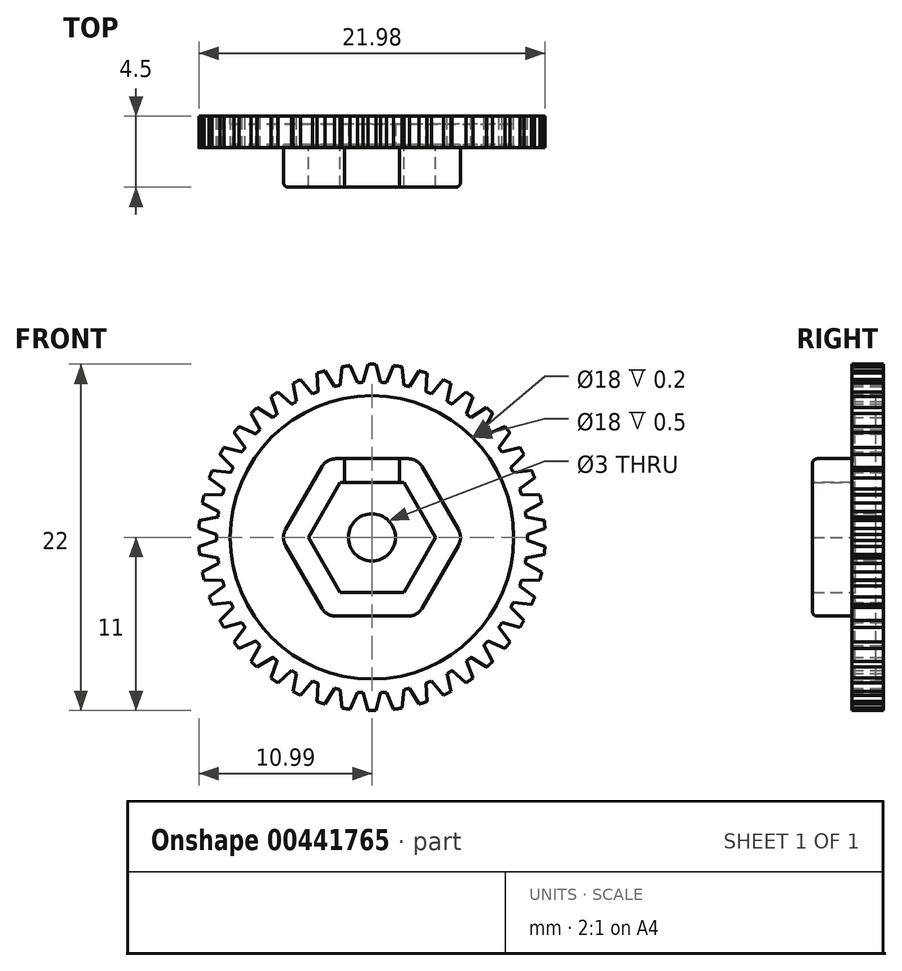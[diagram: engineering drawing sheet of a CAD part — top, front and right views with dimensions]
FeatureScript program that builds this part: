
annotation { "Feature Type Name" : "Feature", "Feature Type Description" : "" }
export const myFeature = defineFeature(function(context is Context, id is Id, definition is map)
    precondition{}
    {
        {
            var Q0;
            Q0=qCreatedBy(makeId("Front.planeOp"),FACE);
            var sketch = newSketch(context, id + "F0", { "sketchPlane" : qUnion([Q0])});
            skCircle(sketch, "E0", {"center": v(0, 0) * mm, "radius": 9.88 * mm});
            skSolve(sketch);
        }
        {
            var Q0;
            Q0=qSketchRegion(id+"F0",true);
            extrude(context, id + "F1", {"entities" : qUnion([Q0]), "depth" : 2 * mm});
        }
        {
            var Q0;
            Q0=qCreatedBy(makeId("Front.planeOp"),FACE);
            var sketch = newSketch(context, id + "F2", { "sketchPlane" : qUnion([Q0])});
            skArc(sketch, "E1", {"start": v(0, 12) * mm, "mid": v(-0.22, 12) * mm, "end": v(-0.45, 12) * mm});
            skArc(sketch, "E2", {"start": v(0.26, 11) * mm, "mid": v(-0.08, 11) * mm, "end": v(-0.41, 11) * mm});
            skArc(sketch, "E3", {"start": v(0.4, 10.5) * mm, "mid": v(0, 10.5) * mm, "end": v(-0.4, 10.5) * mm});
            skCircle(sketch, "E4", {"center": v(0, 0) * mm, "radius": 9.88 * mm});
            skLineSegment(sketch, "E5", {"start": v(0, 0) * mm, "end": v(0, 15.41) * mm});
            skLineSegment(sketch, "E6", {"start": v(0, 0) * mm, "end": v(-0.5, 13.31) * mm});
            skLineSegment(sketch, "E7", {"start": v(-0.4, 10.5) * mm, "end": v(-0.56, 9.86) * mm});
            skLineSegment(sketch, "E8", {"start": v(0.4, 10.5) * mm, "end": v(0.56, 9.86) * mm});
            skLineSegment(sketch, "E9", {"start": v(-0.4, 10.5) * mm, "end": v(-0.26, 11) * mm});
            skLineSegment(sketch, "E10", {"start": v(-0.26, 11) * mm, "end": v(0, 12) * mm});
            skLineSegment(sketch, "E11", {"start": v(0, 12) * mm, "end": v(0.26, 11) * mm});
            skLineSegment(sketch, "E12", {"start": v(0.26, 11) * mm, "end": v(0.4, 10.5) * mm});
            skLineSegment(sketch, "E13.1.0", {"start": v(-1.95, 10.32) * mm, "end": v(-2.02, 9.67) * mm});
            skLineSegment(sketch, "E13.1.1", {"start": v(-1.95, 10.32) * mm, "end": v(-1.9, 10.84) * mm});
            skLineSegment(sketch, "E13.1.2", {"start": v(-1.38, 10.91) * mm, "end": v(-1.18, 10.43) * mm});
            skLineSegment(sketch, "E13.1.3", {"start": v(-1.18, 10.43) * mm, "end": v(-0.92, 9.83) * mm});
            skArc(sketch, "E13.1.4", {"start": v(-1.38, 10.91) * mm, "mid": v(-1.71, 10.87) * mm, "end": v(-2.05, 10.8) * mm});
            skLineSegment(sketch, "E13.2.0", {"start": v(-3.47, 9.91) * mm, "end": v(-3.44, 9.26) * mm});
            skLineSegment(sketch, "E13.2.1", {"start": v(-3.47, 9.91) * mm, "end": v(-3.5, 10.43) * mm});
            skLineSegment(sketch, "E13.2.2", {"start": v(-3, 10.59) * mm, "end": v(-2.72, 10.14) * mm});
            skLineSegment(sketch, "E13.2.3", {"start": v(-2.72, 10.14) * mm, "end": v(-2.37, 9.59) * mm});
            skArc(sketch, "E13.2.4", {"start": v(-3, 10.59) * mm, "mid": v(-3.31, 10.49) * mm, "end": v(-3.63, 10.38) * mm});
            skLineSegment(sketch, "E13.3.0", {"start": v(-4.9, 9.28) * mm, "end": v(-4.78, 8.64) * mm});
            skLineSegment(sketch, "E13.3.1", {"start": v(-4.9, 9.28) * mm, "end": v(-5, 9.8) * mm});
            skLineSegment(sketch, "E13.3.2", {"start": v(-4.54, 10.02) * mm, "end": v(-4.2, 9.62) * mm});
            skLineSegment(sketch, "E13.3.3", {"start": v(-4.2, 9.62) * mm, "end": v(-3.78, 9.12) * mm});
            skArc(sketch, "E13.3.4", {"start": v(-4.54, 10.02) * mm, "mid": v(-4.84, 9.88) * mm, "end": v(-5.14, 9.73) * mm});
            skLineSegment(sketch, "E13.4.0", {"start": v(-6.24, 8.45) * mm, "end": v(-6.01, 7.83) * mm});
            skLineSegment(sketch, "E13.4.1", {"start": v(-6.24, 8.45) * mm, "end": v(-6.41, 8.94) * mm});
            skLineSegment(sketch, "E13.4.2", {"start": v(-5.98, 9.23) * mm, "end": v(-5.59, 8.9) * mm});
            skLineSegment(sketch, "E13.4.3", {"start": v(-5.59, 8.9) * mm, "end": v(-5.1, 8.46) * mm});
            skArc(sketch, "E13.4.4", {"start": v(-5.98, 9.23) * mm, "mid": v(-6.26, 9.05) * mm, "end": v(-6.53, 8.85) * mm});
            skLineSegment(sketch, "E13.5.0", {"start": v(-7.42, 7.42) * mm, "end": v(-7.11, 6.85) * mm});
            skLineSegment(sketch, "E13.5.1", {"start": v(-7.42, 7.42) * mm, "end": v(-7.67, 7.88) * mm});
            skLineSegment(sketch, "E13.5.2", {"start": v(-7.29, 8.24) * mm, "end": v(-6.85, 7.96) * mm});
            skLineSegment(sketch, "E13.5.3", {"start": v(-6.85, 7.96) * mm, "end": v(-6.3, 7.6) * mm});
            skArc(sketch, "E13.5.4", {"start": v(-7.29, 8.24) * mm, "mid": v(-7.54, 8.01) * mm, "end": v(-7.78, 7.78) * mm});
            skLineSegment(sketch, "E13.6.0", {"start": v(-8.45, 6.24) * mm, "end": v(-8.06, 5.71) * mm});
            skLineSegment(sketch, "E13.6.1", {"start": v(-8.45, 6.24) * mm, "end": v(-8.76, 6.65) * mm});
            skLineSegment(sketch, "E13.6.2", {"start": v(-8.43, 7.06) * mm, "end": v(-7.96, 6.85) * mm});
            skLineSegment(sketch, "E13.6.3", {"start": v(-7.96, 6.85) * mm, "end": v(-7.36, 6.58) * mm});
            skArc(sketch, "E13.6.4", {"start": v(-8.43, 7.06) * mm, "mid": v(-8.65, 6.8) * mm, "end": v(-8.85, 6.53) * mm});
            skLineSegment(sketch, "E13.7.0", {"start": v(-9.28, 4.9) * mm, "end": v(-8.82, 4.45) * mm});
            skLineSegment(sketch, "E13.7.1", {"start": v(-9.28, 4.9) * mm, "end": v(-9.65, 5.27) * mm});
            skLineSegment(sketch, "E13.7.2", {"start": v(-9.4, 5.72) * mm, "end": v(-8.9, 5.59) * mm});
            skLineSegment(sketch, "E13.7.3", {"start": v(-8.9, 5.59) * mm, "end": v(-8.26, 5.41) * mm});
            skArc(sketch, "E13.7.4", {"start": v(-9.4, 5.72) * mm, "mid": v(-9.56, 5.43) * mm, "end": v(-9.73, 5.14) * mm});
            skLineSegment(sketch, "E13.8.0", {"start": v(-9.91, 3.47) * mm, "end": v(-9.38, 3.08) * mm});
            skLineSegment(sketch, "E13.8.1", {"start": v(-9.91, 3.47) * mm, "end": v(-10.33, 3.77) * mm});
            skLineSegment(sketch, "E13.8.2", {"start": v(-10.14, 4.26) * mm, "end": v(-9.62, 4.2) * mm});
            skLineSegment(sketch, "E13.8.3", {"start": v(-9.62, 4.2) * mm, "end": v(-8.97, 4.12) * mm});
            skArc(sketch, "E13.8.4", {"start": v(-10.14, 4.26) * mm, "mid": v(-10.27, 3.95) * mm, "end": v(-10.38, 3.63) * mm});
            skLineSegment(sketch, "E13.9.0", {"start": v(-10.32, 1.95) * mm, "end": v(-9.74, 1.65) * mm});
            skLineSegment(sketch, "E13.9.1", {"start": v(-10.32, 1.95) * mm, "end": v(-10.78, 2.2) * mm});
            skLineSegment(sketch, "E13.9.2", {"start": v(-10.66, 2.7) * mm, "end": v(-10.14, 2.72) * mm});
            skLineSegment(sketch, "E13.9.3", {"start": v(-10.14, 2.72) * mm, "end": v(-9.49, 2.74) * mm});
            skArc(sketch, "E13.9.4", {"start": v(-10.66, 2.7) * mm, "mid": v(-10.74, 2.37) * mm, "end": v(-10.8, 2.05) * mm});
            skLineSegment(sketch, "E13.10.0", {"start": v(-10.5, 0.4) * mm, "end": v(-9.87, 0.18) * mm});
            skLineSegment(sketch, "E13.10.1", {"start": v(-10.5, 0.4) * mm, "end": v(-10.99, 0.56) * mm});
            skLineSegment(sketch, "E13.10.2", {"start": v(-10.95, 1.08) * mm, "end": v(-10.43, 1.18) * mm});
            skLineSegment(sketch, "E13.10.3", {"start": v(-10.43, 1.18) * mm, "end": v(-9.8, 1.3) * mm});
            skArc(sketch, "E13.10.4", {"start": v(-10.95, 1.08) * mm, "mid": v(-10.97, 0.75) * mm, "end": v(-11, 0.41) * mm});
            skLineSegment(sketch, "E13.11.0", {"start": v(-10.43, -1.18) * mm, "end": v(-9.8, -1.3) * mm});
            skLineSegment(sketch, "E13.11.1", {"start": v(-10.43, -1.18) * mm, "end": v(-10.95, -1.08) * mm});
            skLineSegment(sketch, "E13.11.2", {"start": v(-10.99, -0.56) * mm, "end": v(-10.5, -0.4) * mm});
            skLineSegment(sketch, "E13.11.3", {"start": v(-10.5, -0.4) * mm, "end": v(-9.87, -0.18) * mm});
            skArc(sketch, "E13.11.4", {"start": v(-10.99, -0.56) * mm, "mid": v(-10.96, -0.9) * mm, "end": v(-10.93, -1.23) * mm});
            skLineSegment(sketch, "E13.12.0", {"start": v(-10.14, -2.72) * mm, "end": v(-9.49, -2.74) * mm});
            skLineSegment(sketch, "E13.12.1", {"start": v(-10.14, -2.72) * mm, "end": v(-10.66, -2.7) * mm});
            skLineSegment(sketch, "E13.12.2", {"start": v(-10.78, -2.2) * mm, "end": v(-10.32, -1.95) * mm});
            skLineSegment(sketch, "E13.12.3", {"start": v(-10.32, -1.95) * mm, "end": v(-9.74, -1.65) * mm});
            skArc(sketch, "E13.12.4", {"start": v(-10.78, -2.2) * mm, "mid": v(-10.7, -2.52) * mm, "end": v(-10.63, -2.85) * mm});
            skLineSegment(sketch, "E13.13.0", {"start": v(-9.62, -4.2) * mm, "end": v(-8.97, -4.12) * mm});
            skLineSegment(sketch, "E13.13.1", {"start": v(-9.62, -4.2) * mm, "end": v(-10.14, -4.26) * mm});
            skLineSegment(sketch, "E13.13.2", {"start": v(-10.33, -3.77) * mm, "end": v(-9.91, -3.47) * mm});
            skLineSegment(sketch, "E13.13.3", {"start": v(-9.91, -3.47) * mm, "end": v(-9.38, -3.08) * mm});
            skArc(sketch, "E13.13.4", {"start": v(-10.33, -3.77) * mm, "mid": v(-10.21, -4.09) * mm, "end": v(-10.08, -4.4) * mm});
            skLineSegment(sketch, "E13.14.0", {"start": v(-8.9, -5.59) * mm, "end": v(-8.26, -5.41) * mm});
            skLineSegment(sketch, "E13.14.1", {"start": v(-8.9, -5.59) * mm, "end": v(-9.4, -5.72) * mm});
            skLineSegment(sketch, "E13.14.2", {"start": v(-9.65, -5.27) * mm, "end": v(-9.28, -4.9) * mm});
            skLineSegment(sketch, "E13.14.3", {"start": v(-9.28, -4.9) * mm, "end": v(-8.82, -4.45) * mm});
            skArc(sketch, "E13.14.4", {"start": v(-9.65, -5.27) * mm, "mid": v(-9.49, -5.56) * mm, "end": v(-9.31, -5.85) * mm});
            skLineSegment(sketch, "E13.15.0", {"start": v(-7.96, -6.85) * mm, "end": v(-7.36, -6.58) * mm});
            skLineSegment(sketch, "E13.15.1", {"start": v(-7.96, -6.85) * mm, "end": v(-8.43, -7.06) * mm});
            skLineSegment(sketch, "E13.15.2", {"start": v(-8.76, -6.65) * mm, "end": v(-8.45, -6.24) * mm});
            skLineSegment(sketch, "E13.15.3", {"start": v(-8.45, -6.24) * mm, "end": v(-8.06, -5.71) * mm});
            skArc(sketch, "E13.15.4", {"start": v(-8.76, -6.65) * mm, "mid": v(-8.55, -6.92) * mm, "end": v(-8.34, -7.18) * mm});
            skLineSegment(sketch, "E13.16.0", {"start": v(-6.85, -7.96) * mm, "end": v(-6.3, -7.6) * mm});
            skLineSegment(sketch, "E13.16.1", {"start": v(-6.85, -7.96) * mm, "end": v(-7.29, -8.24) * mm});
            skLineSegment(sketch, "E13.16.2", {"start": v(-7.67, -7.88) * mm, "end": v(-7.42, -7.42) * mm});
            skLineSegment(sketch, "E13.16.3", {"start": v(-7.42, -7.42) * mm, "end": v(-7.11, -6.85) * mm});
            skArc(sketch, "E13.16.4", {"start": v(-7.67, -7.88) * mm, "mid": v(-7.43, -8.11) * mm, "end": v(-7.18, -8.34) * mm});
            skLineSegment(sketch, "E13.17.0", {"start": v(-5.59, -8.9) * mm, "end": v(-5.1, -8.46) * mm});
            skLineSegment(sketch, "E13.17.1", {"start": v(-5.59, -8.9) * mm, "end": v(-5.98, -9.23) * mm});
            skLineSegment(sketch, "E13.17.2", {"start": v(-6.41, -8.94) * mm, "end": v(-6.24, -8.45) * mm});
            skLineSegment(sketch, "E13.17.3", {"start": v(-6.24, -8.45) * mm, "end": v(-6.01, -7.83) * mm});
            skArc(sketch, "E13.17.4", {"start": v(-6.41, -8.94) * mm, "mid": v(-6.13, -9.13) * mm, "end": v(-5.85, -9.31) * mm});
            skLineSegment(sketch, "E13.18.0", {"start": v(-4.2, -9.62) * mm, "end": v(-3.78, -9.12) * mm});
            skLineSegment(sketch, "E13.18.1", {"start": v(-4.2, -9.62) * mm, "end": v(-4.54, -10.02) * mm});
            skLineSegment(sketch, "E13.18.2", {"start": v(-5, -9.8) * mm, "end": v(-4.9, -9.28) * mm});
            skLineSegment(sketch, "E13.18.3", {"start": v(-4.9, -9.28) * mm, "end": v(-4.78, -8.64) * mm});
            skArc(sketch, "E13.18.4", {"start": v(-5, -9.8) * mm, "mid": v(-4.7, -9.94) * mm, "end": v(-4.4, -10.08) * mm});
            skLineSegment(sketch, "E13.19.0", {"start": v(-2.72, -10.14) * mm, "end": v(-2.37, -9.59) * mm});
            skLineSegment(sketch, "E13.19.1", {"start": v(-2.72, -10.14) * mm, "end": v(-3, -10.59) * mm});
            skLineSegment(sketch, "E13.19.2", {"start": v(-3.5, -10.43) * mm, "end": v(-3.47, -9.91) * mm});
            skLineSegment(sketch, "E13.19.3", {"start": v(-3.47, -9.91) * mm, "end": v(-3.44, -9.26) * mm});
            skArc(sketch, "E13.19.4", {"start": v(-3.5, -10.43) * mm, "mid": v(-3.17, -10.53) * mm, "end": v(-2.85, -10.63) * mm});
            skLineSegment(sketch, "E13.20.0", {"start": v(-1.18, -10.43) * mm, "end": v(-0.92, -9.83) * mm});
            skLineSegment(sketch, "E13.20.1", {"start": v(-1.18, -10.43) * mm, "end": v(-1.38, -10.91) * mm});
            skLineSegment(sketch, "E13.20.2", {"start": v(-1.9, -10.84) * mm, "end": v(-1.95, -10.32) * mm});
            skLineSegment(sketch, "E13.20.3", {"start": v(-1.95, -10.32) * mm, "end": v(-2.02, -9.67) * mm});
            skArc(sketch, "E13.20.4", {"start": v(-1.9, -10.84) * mm, "mid": v(-1.57, -10.89) * mm, "end": v(-1.23, -10.93) * mm});
            skLineSegment(sketch, "E13.21.0", {"start": v(0.4, -10.5) * mm, "end": v(0.56, -9.86) * mm});
            skLineSegment(sketch, "E13.21.1", {"start": v(0.4, -10.5) * mm, "end": v(0.26, -11) * mm});
            skLineSegment(sketch, "E13.21.2", {"start": v(-0.26, -11) * mm, "end": v(-0.4, -10.5) * mm});
            skLineSegment(sketch, "E13.21.3", {"start": v(-0.4, -10.5) * mm, "end": v(-0.56, -9.86) * mm});
            skArc(sketch, "E13.21.4", {"start": v(-0.26, -11) * mm, "mid": v(0.08, -11) * mm, "end": v(0.41, -11) * mm});
            skLineSegment(sketch, "E13.22.0", {"start": v(1.95, -10.32) * mm, "end": v(2.02, -9.67) * mm});
            skLineSegment(sketch, "E13.22.1", {"start": v(1.95, -10.32) * mm, "end": v(1.9, -10.84) * mm});
            skLineSegment(sketch, "E13.22.2", {"start": v(1.38, -10.91) * mm, "end": v(1.18, -10.43) * mm});
            skLineSegment(sketch, "E13.22.3", {"start": v(1.18, -10.43) * mm, "end": v(0.92, -9.83) * mm});
            skArc(sketch, "E13.22.4", {"start": v(1.38, -10.91) * mm, "mid": v(1.71, -10.87) * mm, "end": v(2.05, -10.8) * mm});
            skLineSegment(sketch, "E13.23.0", {"start": v(3.47, -9.91) * mm, "end": v(3.44, -9.26) * mm});
            skLineSegment(sketch, "E13.23.1", {"start": v(3.47, -9.91) * mm, "end": v(3.5, -10.43) * mm});
            skLineSegment(sketch, "E13.23.2", {"start": v(3, -10.59) * mm, "end": v(2.72, -10.14) * mm});
            skLineSegment(sketch, "E13.23.3", {"start": v(2.72, -10.14) * mm, "end": v(2.37, -9.59) * mm});
            skArc(sketch, "E13.23.4", {"start": v(3, -10.59) * mm, "mid": v(3.31, -10.49) * mm, "end": v(3.63, -10.38) * mm});
            skLineSegment(sketch, "E13.24.0", {"start": v(4.9, -9.28) * mm, "end": v(4.78, -8.64) * mm});
            skLineSegment(sketch, "E13.24.1", {"start": v(4.9, -9.28) * mm, "end": v(5, -9.8) * mm});
            skLineSegment(sketch, "E13.24.2", {"start": v(4.54, -10.02) * mm, "end": v(4.2, -9.62) * mm});
            skLineSegment(sketch, "E13.24.3", {"start": v(4.2, -9.62) * mm, "end": v(3.78, -9.12) * mm});
            skArc(sketch, "E13.24.4", {"start": v(4.54, -10.02) * mm, "mid": v(4.84, -9.88) * mm, "end": v(5.14, -9.73) * mm});
            skLineSegment(sketch, "E13.25.0", {"start": v(6.24, -8.45) * mm, "end": v(6.01, -7.83) * mm});
            skLineSegment(sketch, "E13.25.1", {"start": v(6.24, -8.45) * mm, "end": v(6.41, -8.94) * mm});
            skLineSegment(sketch, "E13.25.2", {"start": v(5.98, -9.23) * mm, "end": v(5.59, -8.9) * mm});
            skLineSegment(sketch, "E13.25.3", {"start": v(5.59, -8.9) * mm, "end": v(5.1, -8.46) * mm});
            skArc(sketch, "E13.25.4", {"start": v(5.98, -9.23) * mm, "mid": v(6.26, -9.05) * mm, "end": v(6.53, -8.85) * mm});
            skLineSegment(sketch, "E13.26.0", {"start": v(7.42, -7.42) * mm, "end": v(7.11, -6.85) * mm});
            skLineSegment(sketch, "E13.26.1", {"start": v(7.42, -7.42) * mm, "end": v(7.67, -7.88) * mm});
            skLineSegment(sketch, "E13.26.2", {"start": v(7.29, -8.24) * mm, "end": v(6.85, -7.96) * mm});
            skLineSegment(sketch, "E13.26.3", {"start": v(6.85, -7.96) * mm, "end": v(6.3, -7.6) * mm});
            skArc(sketch, "E13.26.4", {"start": v(7.29, -8.24) * mm, "mid": v(7.54, -8.01) * mm, "end": v(7.78, -7.78) * mm});
            skLineSegment(sketch, "E13.27.0", {"start": v(8.45, -6.24) * mm, "end": v(8.06, -5.71) * mm});
            skLineSegment(sketch, "E13.27.1", {"start": v(8.45, -6.24) * mm, "end": v(8.76, -6.65) * mm});
            skLineSegment(sketch, "E13.27.2", {"start": v(8.43, -7.06) * mm, "end": v(7.96, -6.85) * mm});
            skLineSegment(sketch, "E13.27.3", {"start": v(7.96, -6.85) * mm, "end": v(7.36, -6.58) * mm});
            skArc(sketch, "E13.27.4", {"start": v(8.43, -7.06) * mm, "mid": v(8.65, -6.8) * mm, "end": v(8.85, -6.53) * mm});
            skLineSegment(sketch, "E13.28.0", {"start": v(9.28, -4.9) * mm, "end": v(8.82, -4.45) * mm});
            skLineSegment(sketch, "E13.28.1", {"start": v(9.28, -4.9) * mm, "end": v(9.65, -5.27) * mm});
            skLineSegment(sketch, "E13.28.2", {"start": v(9.4, -5.72) * mm, "end": v(8.9, -5.59) * mm});
            skLineSegment(sketch, "E13.28.3", {"start": v(8.9, -5.59) * mm, "end": v(8.26, -5.41) * mm});
            skArc(sketch, "E13.28.4", {"start": v(9.4, -5.72) * mm, "mid": v(9.56, -5.43) * mm, "end": v(9.73, -5.14) * mm});
            skLineSegment(sketch, "E13.29.0", {"start": v(9.91, -3.47) * mm, "end": v(9.38, -3.08) * mm});
            skLineSegment(sketch, "E13.29.1", {"start": v(9.91, -3.47) * mm, "end": v(10.33, -3.77) * mm});
            skLineSegment(sketch, "E13.29.2", {"start": v(10.14, -4.26) * mm, "end": v(9.62, -4.2) * mm});
            skLineSegment(sketch, "E13.29.3", {"start": v(9.62, -4.2) * mm, "end": v(8.97, -4.12) * mm});
            skArc(sketch, "E13.29.4", {"start": v(10.14, -4.26) * mm, "mid": v(10.27, -3.95) * mm, "end": v(10.38, -3.63) * mm});
            skLineSegment(sketch, "E13.30.0", {"start": v(10.32, -1.95) * mm, "end": v(9.74, -1.65) * mm});
            skLineSegment(sketch, "E13.30.1", {"start": v(10.32, -1.95) * mm, "end": v(10.78, -2.2) * mm});
            skLineSegment(sketch, "E13.30.2", {"start": v(10.66, -2.7) * mm, "end": v(10.14, -2.72) * mm});
            skLineSegment(sketch, "E13.30.3", {"start": v(10.14, -2.72) * mm, "end": v(9.49, -2.74) * mm});
            skArc(sketch, "E13.30.4", {"start": v(10.66, -2.7) * mm, "mid": v(10.74, -2.37) * mm, "end": v(10.8, -2.05) * mm});
            skLineSegment(sketch, "E13.31.0", {"start": v(10.5, -0.4) * mm, "end": v(9.87, -0.18) * mm});
            skLineSegment(sketch, "E13.31.1", {"start": v(10.5, -0.4) * mm, "end": v(10.99, -0.56) * mm});
            skLineSegment(sketch, "E13.31.2", {"start": v(10.95, -1.08) * mm, "end": v(10.43, -1.18) * mm});
            skLineSegment(sketch, "E13.31.3", {"start": v(10.43, -1.18) * mm, "end": v(9.8, -1.3) * mm});
            skArc(sketch, "E13.31.4", {"start": v(10.95, -1.08) * mm, "mid": v(10.97, -0.75) * mm, "end": v(11, -0.41) * mm});
            skLineSegment(sketch, "E13.32.0", {"start": v(10.43, 1.18) * mm, "end": v(9.8, 1.3) * mm});
            skLineSegment(sketch, "E13.32.1", {"start": v(10.43, 1.18) * mm, "end": v(10.95, 1.08) * mm});
            skLineSegment(sketch, "E13.32.2", {"start": v(10.99, 0.56) * mm, "end": v(10.5, 0.4) * mm});
            skLineSegment(sketch, "E13.32.3", {"start": v(10.5, 0.4) * mm, "end": v(9.87, 0.18) * mm});
            skArc(sketch, "E13.32.4", {"start": v(10.99, 0.56) * mm, "mid": v(10.96, 0.9) * mm, "end": v(10.93, 1.23) * mm});
            skLineSegment(sketch, "E13.33.0", {"start": v(10.14, 2.72) * mm, "end": v(9.49, 2.74) * mm});
            skLineSegment(sketch, "E13.33.1", {"start": v(10.14, 2.72) * mm, "end": v(10.66, 2.7) * mm});
            skLineSegment(sketch, "E13.33.2", {"start": v(10.78, 2.2) * mm, "end": v(10.32, 1.95) * mm});
            skLineSegment(sketch, "E13.33.3", {"start": v(10.32, 1.95) * mm, "end": v(9.74, 1.65) * mm});
            skArc(sketch, "E13.33.4", {"start": v(10.78, 2.2) * mm, "mid": v(10.7, 2.52) * mm, "end": v(10.63, 2.85) * mm});
            skLineSegment(sketch, "E13.34.0", {"start": v(9.62, 4.2) * mm, "end": v(8.97, 4.12) * mm});
            skLineSegment(sketch, "E13.34.1", {"start": v(9.62, 4.2) * mm, "end": v(10.14, 4.26) * mm});
            skLineSegment(sketch, "E13.34.2", {"start": v(10.33, 3.77) * mm, "end": v(9.91, 3.47) * mm});
            skLineSegment(sketch, "E13.34.3", {"start": v(9.91, 3.47) * mm, "end": v(9.38, 3.08) * mm});
            skArc(sketch, "E13.34.4", {"start": v(10.33, 3.77) * mm, "mid": v(10.21, 4.09) * mm, "end": v(10.08, 4.4) * mm});
            skLineSegment(sketch, "E13.35.0", {"start": v(8.9, 5.59) * mm, "end": v(8.26, 5.41) * mm});
            skLineSegment(sketch, "E13.35.1", {"start": v(8.9, 5.59) * mm, "end": v(9.4, 5.72) * mm});
            skLineSegment(sketch, "E13.35.2", {"start": v(9.65, 5.27) * mm, "end": v(9.28, 4.9) * mm});
            skLineSegment(sketch, "E13.35.3", {"start": v(9.28, 4.9) * mm, "end": v(8.82, 4.45) * mm});
            skArc(sketch, "E13.35.4", {"start": v(9.65, 5.27) * mm, "mid": v(9.49, 5.56) * mm, "end": v(9.31, 5.85) * mm});
            skLineSegment(sketch, "E13.36.0", {"start": v(7.96, 6.85) * mm, "end": v(7.36, 6.58) * mm});
            skLineSegment(sketch, "E13.36.1", {"start": v(7.96, 6.85) * mm, "end": v(8.43, 7.06) * mm});
            skLineSegment(sketch, "E13.36.2", {"start": v(8.76, 6.65) * mm, "end": v(8.45, 6.24) * mm});
            skLineSegment(sketch, "E13.36.3", {"start": v(8.45, 6.24) * mm, "end": v(8.06, 5.71) * mm});
            skArc(sketch, "E13.36.4", {"start": v(8.76, 6.65) * mm, "mid": v(8.55, 6.92) * mm, "end": v(8.34, 7.18) * mm});
            skLineSegment(sketch, "E13.37.0", {"start": v(6.85, 7.96) * mm, "end": v(6.3, 7.6) * mm});
            skLineSegment(sketch, "E13.37.1", {"start": v(6.85, 7.96) * mm, "end": v(7.29, 8.24) * mm});
            skLineSegment(sketch, "E13.37.2", {"start": v(7.67, 7.88) * mm, "end": v(7.42, 7.42) * mm});
            skLineSegment(sketch, "E13.37.3", {"start": v(7.42, 7.42) * mm, "end": v(7.11, 6.85) * mm});
            skArc(sketch, "E13.37.4", {"start": v(7.67, 7.88) * mm, "mid": v(7.43, 8.11) * mm, "end": v(7.18, 8.34) * mm});
            skLineSegment(sketch, "E13.38.0", {"start": v(5.59, 8.9) * mm, "end": v(5.1, 8.46) * mm});
            skLineSegment(sketch, "E13.38.1", {"start": v(5.59, 8.9) * mm, "end": v(5.98, 9.23) * mm});
            skLineSegment(sketch, "E13.38.2", {"start": v(6.41, 8.94) * mm, "end": v(6.24, 8.45) * mm});
            skLineSegment(sketch, "E13.38.3", {"start": v(6.24, 8.45) * mm, "end": v(6.01, 7.83) * mm});
            skArc(sketch, "E13.38.4", {"start": v(6.41, 8.94) * mm, "mid": v(6.13, 9.13) * mm, "end": v(5.85, 9.31) * mm});
            skLineSegment(sketch, "E13.39.0", {"start": v(4.2, 9.62) * mm, "end": v(3.78, 9.12) * mm});
            skLineSegment(sketch, "E13.39.1", {"start": v(4.2, 9.62) * mm, "end": v(4.54, 10.02) * mm});
            skLineSegment(sketch, "E13.39.2", {"start": v(5, 9.8) * mm, "end": v(4.9, 9.28) * mm});
            skLineSegment(sketch, "E13.39.3", {"start": v(4.9, 9.28) * mm, "end": v(4.78, 8.64) * mm});
            skArc(sketch, "E13.39.4", {"start": v(5, 9.8) * mm, "mid": v(4.7, 9.94) * mm, "end": v(4.4, 10.08) * mm});
            skLineSegment(sketch, "E13.40.0", {"start": v(2.72, 10.14) * mm, "end": v(2.37, 9.59) * mm});
            skLineSegment(sketch, "E13.40.1", {"start": v(2.72, 10.14) * mm, "end": v(3, 10.59) * mm});
            skLineSegment(sketch, "E13.40.2", {"start": v(3.5, 10.43) * mm, "end": v(3.47, 9.91) * mm});
            skLineSegment(sketch, "E13.40.3", {"start": v(3.47, 9.91) * mm, "end": v(3.44, 9.26) * mm});
            skArc(sketch, "E13.40.4", {"start": v(3.5, 10.43) * mm, "mid": v(3.17, 10.53) * mm, "end": v(2.85, 10.63) * mm});
            skLineSegment(sketch, "E13.41.0", {"start": v(1.18, 10.43) * mm, "end": v(0.92, 9.83) * mm});
            skLineSegment(sketch, "E13.41.1", {"start": v(1.18, 10.43) * mm, "end": v(1.38, 10.91) * mm});
            skLineSegment(sketch, "E13.41.2", {"start": v(1.9, 10.84) * mm, "end": v(1.95, 10.32) * mm});
            skLineSegment(sketch, "E13.41.3", {"start": v(1.95, 10.32) * mm, "end": v(2.02, 9.67) * mm});
            skArc(sketch, "E13.41.4", {"start": v(1.9, 10.84) * mm, "mid": v(1.57, 10.89) * mm, "end": v(1.23, 10.93) * mm});
            skSolve(sketch);
        }
        {
            var Q0;
            {var subQ2=sQuery(id+"F2.wireOp",EDGE,"E13.32.0");Q0=makeQuery(id+"F2.imprint","IMPRINT",FACE,{"disambiguationData":[TD([[makeQuery(id+"F2.imprint","IMPRINT",EDGE,{"derivedFrom":subQ2}),1.0]])]});}
            var Q1;
            {var subQ1=sQuery(id+"F2.wireOp",EDGE,"E13.33.0");Q1=makeQuery(id+"F2.imprint","IMPRINT",FACE,{"disambiguationData":[TD([[makeQuery(id+"F2.imprint","IMPRINT",EDGE,{"derivedFrom":subQ1}),1.0]])]});}
            var Q2;
            {var subQ2=sQuery(id+"F2.wireOp",EDGE,"E13.34.0");Q2=makeQuery(id+"F2.imprint","IMPRINT",FACE,{"disambiguationData":[TD([[makeQuery(id+"F2.imprint","IMPRINT",EDGE,{"derivedFrom":subQ2}),1.0]])]});}
            var Q3;
            {var subQ1=sQuery(id+"F2.wireOp",EDGE,"E13.35.0");Q3=makeQuery(id+"F2.imprint","IMPRINT",FACE,{"disambiguationData":[TD([[makeQuery(id+"F2.imprint","IMPRINT",EDGE,{"derivedFrom":subQ1}),1.0]])]});}
            var Q4;
            {var subQ2=sQuery(id+"F2.wireOp",EDGE,"E13.36.0");Q4=makeQuery(id+"F2.imprint","IMPRINT",FACE,{"disambiguationData":[TD([[makeQuery(id+"F2.imprint","IMPRINT",EDGE,{"derivedFrom":subQ2}),1.0]])]});}
            var Q5;
            {var subQ2=sQuery(id+"F2.wireOp",EDGE,"E13.37.0");Q5=makeQuery(id+"F2.imprint","IMPRINT",FACE,{"disambiguationData":[TD([[makeQuery(id+"F2.imprint","IMPRINT",EDGE,{"derivedFrom":subQ2}),1.0]])]});}
            var Q6;
            {var subQ1=sQuery(id+"F2.wireOp",EDGE,"E13.38.0");Q6=makeQuery(id+"F2.imprint","IMPRINT",FACE,{"disambiguationData":[TD([[makeQuery(id+"F2.imprint","IMPRINT",EDGE,{"derivedFrom":subQ1}),1.0]])]});}
            var Q7;
            {var subQ2=sQuery(id+"F2.wireOp",EDGE,"E13.39.0");Q7=makeQuery(id+"F2.imprint","IMPRINT",FACE,{"disambiguationData":[TD([[makeQuery(id+"F2.imprint","IMPRINT",EDGE,{"derivedFrom":subQ2}),1.0]])]});}
            var Q8;
            {var subQ1=sQuery(id+"F2.wireOp",EDGE,"E13.40.0");Q8=makeQuery(id+"F2.imprint","IMPRINT",FACE,{"disambiguationData":[TD([[makeQuery(id+"F2.imprint","IMPRINT",EDGE,{"derivedFrom":subQ1}),1.0]])]});}
            var Q9;
            {var subQ2=sQuery(id+"F2.wireOp",EDGE,"E13.41.0");Q9=makeQuery(id+"F2.imprint","IMPRINT",FACE,{"disambiguationData":[TD([[makeQuery(id+"F2.imprint","IMPRINT",EDGE,{"derivedFrom":subQ2}),1.0]])]});}
            var Q10;
            {var subQ2=sQuery(id+"F2.wireOp",EDGE,"E13.1.0");Q10=makeQuery(id+"F2.imprint","IMPRINT",FACE,{"disambiguationData":[TD([[makeQuery(id+"F2.imprint","IMPRINT",EDGE,{"derivedFrom":subQ2}),1.0]])]});}
            var Q11;
            {var subQ1=sQuery(id+"F2.wireOp",EDGE,"E13.2.0");Q11=makeQuery(id+"F2.imprint","IMPRINT",FACE,{"disambiguationData":[TD([[makeQuery(id+"F2.imprint","IMPRINT",EDGE,{"derivedFrom":subQ1}),1.0]])]});}
            var Q12;
            {var subQ2=sQuery(id+"F2.wireOp",EDGE,"E13.3.0");Q12=makeQuery(id+"F2.imprint","IMPRINT",FACE,{"disambiguationData":[TD([[makeQuery(id+"F2.imprint","IMPRINT",EDGE,{"derivedFrom":subQ2}),1.0]])]});}
            var Q13;
            {var subQ2=sQuery(id+"F2.wireOp",EDGE,"E13.4.0");Q13=makeQuery(id+"F2.imprint","IMPRINT",FACE,{"disambiguationData":[TD([[makeQuery(id+"F2.imprint","IMPRINT",EDGE,{"derivedFrom":subQ2}),1.0]])]});}
            var Q14;
            {var subQ1=sQuery(id+"F2.wireOp",EDGE,"E13.5.0");Q14=makeQuery(id+"F2.imprint","IMPRINT",FACE,{"disambiguationData":[TD([[makeQuery(id+"F2.imprint","IMPRINT",EDGE,{"derivedFrom":subQ1}),1.0]])]});}
            var Q15;
            {var subQ2=sQuery(id+"F2.wireOp",EDGE,"E13.6.0");Q15=makeQuery(id+"F2.imprint","IMPRINT",FACE,{"disambiguationData":[TD([[makeQuery(id+"F2.imprint","IMPRINT",EDGE,{"derivedFrom":subQ2}),1.0]])]});}
            var Q16;
            {var subQ1=sQuery(id+"F2.wireOp",EDGE,"E13.7.0");Q16=makeQuery(id+"F2.imprint","IMPRINT",FACE,{"disambiguationData":[TD([[makeQuery(id+"F2.imprint","IMPRINT",EDGE,{"derivedFrom":subQ1}),1.0]])]});}
            var Q17;
            {var subQ1=sQuery(id+"F2.wireOp",EDGE,"E13.8.0");Q17=makeQuery(id+"F2.imprint","IMPRINT",FACE,{"disambiguationData":[TD([[makeQuery(id+"F2.imprint","IMPRINT",EDGE,{"derivedFrom":subQ1}),1.0]])]});}
            var Q18;
            {var subQ2=sQuery(id+"F2.wireOp",EDGE,"E13.9.0");Q18=makeQuery(id+"F2.imprint","IMPRINT",FACE,{"disambiguationData":[TD([[makeQuery(id+"F2.imprint","IMPRINT",EDGE,{"derivedFrom":subQ2}),1.0]])]});}
            var Q19;
            {var subQ1=sQuery(id+"F2.wireOp",EDGE,"E13.10.0");Q19=makeQuery(id+"F2.imprint","IMPRINT",FACE,{"disambiguationData":[TD([[makeQuery(id+"F2.imprint","IMPRINT",EDGE,{"derivedFrom":subQ1}),1.0]])]});}
            var Q20;
            {var subQ2=sQuery(id+"F2.wireOp",EDGE,"E13.11.0");Q20=makeQuery(id+"F2.imprint","IMPRINT",FACE,{"disambiguationData":[TD([[makeQuery(id+"F2.imprint","IMPRINT",EDGE,{"derivedFrom":subQ2}),1.0]])]});}
            var Q21;
            {var subQ1=sQuery(id+"F2.wireOp",EDGE,"E13.12.0");Q21=makeQuery(id+"F2.imprint","IMPRINT",FACE,{"disambiguationData":[TD([[makeQuery(id+"F2.imprint","IMPRINT",EDGE,{"derivedFrom":subQ1}),1.0]])]});}
            var Q22;
            {var subQ2=sQuery(id+"F2.wireOp",EDGE,"E13.13.0");Q22=makeQuery(id+"F2.imprint","IMPRINT",FACE,{"disambiguationData":[TD([[makeQuery(id+"F2.imprint","IMPRINT",EDGE,{"derivedFrom":subQ2}),1.0]])]});}
            var Q23;
            {var subQ2=sQuery(id+"F2.wireOp",EDGE,"E13.14.0");Q23=makeQuery(id+"F2.imprint","IMPRINT",FACE,{"disambiguationData":[TD([[makeQuery(id+"F2.imprint","IMPRINT",EDGE,{"derivedFrom":subQ2}),1.0]])]});}
            var Q24;
            {var subQ1=sQuery(id+"F2.wireOp",EDGE,"E13.15.0");Q24=makeQuery(id+"F2.imprint","IMPRINT",FACE,{"disambiguationData":[TD([[makeQuery(id+"F2.imprint","IMPRINT",EDGE,{"derivedFrom":subQ1}),1.0]])]});}
            var Q25;
            {var subQ2=sQuery(id+"F2.wireOp",EDGE,"E13.16.0");Q25=makeQuery(id+"F2.imprint","IMPRINT",FACE,{"disambiguationData":[TD([[makeQuery(id+"F2.imprint","IMPRINT",EDGE,{"derivedFrom":subQ2}),1.0]])]});}
            var Q26;
            {var subQ1=sQuery(id+"F2.wireOp",EDGE,"E13.17.0");Q26=makeQuery(id+"F2.imprint","IMPRINT",FACE,{"disambiguationData":[TD([[makeQuery(id+"F2.imprint","IMPRINT",EDGE,{"derivedFrom":subQ1}),1.0]])]});}
            var Q27;
            {var subQ2=sQuery(id+"F2.wireOp",EDGE,"E13.18.0");Q27=makeQuery(id+"F2.imprint","IMPRINT",FACE,{"disambiguationData":[TD([[makeQuery(id+"F2.imprint","IMPRINT",EDGE,{"derivedFrom":subQ2}),1.0]])]});}
            var Q28;
            {var subQ1=sQuery(id+"F2.wireOp",EDGE,"E13.19.0");Q28=makeQuery(id+"F2.imprint","IMPRINT",FACE,{"disambiguationData":[TD([[makeQuery(id+"F2.imprint","IMPRINT",EDGE,{"derivedFrom":subQ1}),1.0]])]});}
            var Q29;
            {var subQ1=sQuery(id+"F2.wireOp",EDGE,"E13.20.0");Q29=makeQuery(id+"F2.imprint","IMPRINT",FACE,{"disambiguationData":[TD([[makeQuery(id+"F2.imprint","IMPRINT",EDGE,{"derivedFrom":subQ1}),1.0]])]});}
            var Q30;
            {var subQ2=sQuery(id+"F2.wireOp",EDGE,"E13.21.0");Q30=makeQuery(id+"F2.imprint","IMPRINT",FACE,{"disambiguationData":[TD([[makeQuery(id+"F2.imprint","IMPRINT",EDGE,{"derivedFrom":subQ2}),1.0]])]});}
            var Q31;
            {var subQ1=sQuery(id+"F2.wireOp",EDGE,"E13.22.0");Q31=makeQuery(id+"F2.imprint","IMPRINT",FACE,{"disambiguationData":[TD([[makeQuery(id+"F2.imprint","IMPRINT",EDGE,{"derivedFrom":subQ1}),1.0]])]});}
            var Q32;
            {var subQ2=sQuery(id+"F2.wireOp",EDGE,"E13.23.0");Q32=makeQuery(id+"F2.imprint","IMPRINT",FACE,{"disambiguationData":[TD([[makeQuery(id+"F2.imprint","IMPRINT",EDGE,{"derivedFrom":subQ2}),1.0]])]});}
            var Q33;
            {var subQ2=sQuery(id+"F2.wireOp",EDGE,"E13.24.0");Q33=makeQuery(id+"F2.imprint","IMPRINT",FACE,{"disambiguationData":[TD([[makeQuery(id+"F2.imprint","IMPRINT",EDGE,{"derivedFrom":subQ2}),1.0]])]});}
            var Q34;
            {var subQ1=sQuery(id+"F2.wireOp",EDGE,"E13.25.0");Q34=makeQuery(id+"F2.imprint","IMPRINT",FACE,{"disambiguationData":[TD([[makeQuery(id+"F2.imprint","IMPRINT",EDGE,{"derivedFrom":subQ1}),1.0]])]});}
            var Q35;
            {var subQ2=sQuery(id+"F2.wireOp",EDGE,"E13.26.0");Q35=makeQuery(id+"F2.imprint","IMPRINT",FACE,{"disambiguationData":[TD([[makeQuery(id+"F2.imprint","IMPRINT",EDGE,{"derivedFrom":subQ2}),1.0]])]});}
            var Q36;
            {var subQ1=sQuery(id+"F2.wireOp",EDGE,"E13.27.0");Q36=makeQuery(id+"F2.imprint","IMPRINT",FACE,{"disambiguationData":[TD([[makeQuery(id+"F2.imprint","IMPRINT",EDGE,{"derivedFrom":subQ1}),1.0]])]});}
            var Q37;
            {var subQ2=sQuery(id+"F2.wireOp",EDGE,"E13.28.0");Q37=makeQuery(id+"F2.imprint","IMPRINT",FACE,{"disambiguationData":[TD([[makeQuery(id+"F2.imprint","IMPRINT",EDGE,{"derivedFrom":subQ2}),1.0]])]});}
            var Q38;
            {var subQ2=sQuery(id+"F2.wireOp",EDGE,"E13.29.0");Q38=makeQuery(id+"F2.imprint","IMPRINT",FACE,{"disambiguationData":[TD([[makeQuery(id+"F2.imprint","IMPRINT",EDGE,{"derivedFrom":subQ2}),1.0]])]});}
            var Q39;
            {var subQ1=sQuery(id+"F2.wireOp",EDGE,"E13.30.0");Q39=makeQuery(id+"F2.imprint","IMPRINT",FACE,{"disambiguationData":[TD([[makeQuery(id+"F2.imprint","IMPRINT",EDGE,{"derivedFrom":subQ1}),1.0]])]});}
            var Q40;
            {var subQ2=sQuery(id+"F2.wireOp",EDGE,"E13.31.0");Q40=makeQuery(id+"F2.imprint","IMPRINT",FACE,{"disambiguationData":[TD([[makeQuery(id+"F2.imprint","IMPRINT",EDGE,{"derivedFrom":subQ2}),1.0]])]});}
            var Q41;
            {var subQ0=sQuery(id+"F2.wireOp",EDGE,"E7");Q41=makeQuery(id+"F2.imprint","IMPRINT",FACE,{"disambiguationData":[TD([[makeQuery(id+"F2.imprint","IMPRINT",EDGE,{"derivedFrom":subQ0}),1.0]])]});}
            var Q42;
            {var subQ0=sQuery(id+"F2.wireOp",EDGE,"E12");Q42=makeQuery(id+"F2.imprint","IMPRINT",FACE,{"disambiguationData":[TD([[makeQuery(id+"F2.imprint","IMPRINT",EDGE,{"derivedFrom":subQ0}),-1.0]])]});}
            var Q43;
            {var subQ0=sQuery(id+"F2.wireOp",EDGE,"E8");Q43=makeQuery(id+"F2.imprint","IMPRINT",FACE,{"disambiguationData":[TD([[makeQuery(id+"F2.imprint","IMPRINT",EDGE,{"derivedFrom":subQ0}),-1.0]])]});}
            var Q44;
            {var subQ0=sQuery(id+"F2.wireOp",EDGE,"E9");Q44=makeQuery(id+"F2.imprint","IMPRINT",FACE,{"disambiguationData":[TD([[makeQuery(id+"F2.imprint","IMPRINT",EDGE,{"derivedFrom":subQ0}),-1.0]])]});}
            var Q45;
            {var subQ3=sQuery(id+"F2.wireOp",EDGE,"E5");var subQ5=sQuery(id+"F2.wireOp",EDGE,"E4");var subQ6=makeQuery(id+"F2.imprint","INTERSECT",VERTEX,{"derivedFrom":[subQ5,subQ3]});Q45=makeQuery(id+"F2.imprint","IMPRINT",FACE,{"disambiguationData":[TD([[makeQuery(id+"F2.imprint","IMPRINT",EDGE,{"disambiguationData":[TD([[subQ6,-1.0]])],"derivedFrom":subQ5}),-1.0]])]});}
            extrude(context, id + "F3", {"entities" : qUnion([Q0, Q1, Q2, Q3, Q4, Q5, Q6, Q7, Q8, Q9, Q10, Q11, Q12, Q13, Q14, Q15, Q16, Q17, Q18, Q19, Q20, Q21, Q22, Q23, Q24, Q25, Q26, Q27, Q28, Q29, Q30, Q31, Q32, Q33, Q34, Q35, Q36, Q37, Q38, Q39, Q40, Q41, Q42, Q43, Q44, Q45]), "operationType" : NewBodyOperationType.ADD, "depth" : 2 * mm});
        }
        {
            var Q0;
            {var subQ0=sQuery(id+"F2.wireOp",EDGE,"E4");Q0=makeQuery(id+"F3.boolean.opBoolean","MERGE",FACE,{"derivedFrom":[makeQuery(id+"F1.opExtrude","CAP_FACE",FACE,{"disambiguationData":[OSD([sQuery(id+"F0.wireOp",EDGE,"E0")])],"isStart":false}),makeQuery(id+"F3.opExtrude","CAP_FACE",FACE,{"disambiguationData":[OSD([sQuery(id+"F2.wireOp",EDGE,"E2"),subQ0,sQuery(id+"F2.wireOp",EDGE,"E7"),sQuery(id+"F2.wireOp",EDGE,"E8"),sQuery(id+"F2.wireOp",EDGE,"E9"),sQuery(id+"F2.wireOp",EDGE,"E12")])],"isStart":false}),makeQuery(id+"F3.opExtrude","CAP_FACE",FACE,{"disambiguationData":[OSD([subQ0,sQuery(id+"F2.wireOp",EDGE,"E13.32.0"),sQuery(id+"F2.wireOp",EDGE,"E13.32.1"),sQuery(id+"F2.wireOp",EDGE,"E13.32.2"),sQuery(id+"F2.wireOp",EDGE,"E13.32.3"),sQuery(id+"F2.wireOp",EDGE,"E13.32.4")])],"isStart":false}),makeQuery(id+"F3.opExtrude","CAP_FACE",FACE,{"disambiguationData":[OSD([subQ0,sQuery(id+"F2.wireOp",EDGE,"E13.33.0"),sQuery(id+"F2.wireOp",EDGE,"E13.33.1"),sQuery(id+"F2.wireOp",EDGE,"E13.33.2"),sQuery(id+"F2.wireOp",EDGE,"E13.33.3"),sQuery(id+"F2.wireOp",EDGE,"E13.33.4")])],"isStart":false}),makeQuery(id+"F3.opExtrude","CAP_FACE",FACE,{"disambiguationData":[OSD([subQ0,sQuery(id+"F2.wireOp",EDGE,"E13.34.0"),sQuery(id+"F2.wireOp",EDGE,"E13.34.1"),sQuery(id+"F2.wireOp",EDGE,"E13.34.2"),sQuery(id+"F2.wireOp",EDGE,"E13.34.3"),sQuery(id+"F2.wireOp",EDGE,"E13.34.4")])],"isStart":false}),makeQuery(id+"F3.opExtrude","CAP_FACE",FACE,{"disambiguationData":[OSD([subQ0,sQuery(id+"F2.wireOp",EDGE,"E13.35.0"),sQuery(id+"F2.wireOp",EDGE,"E13.35.1"),sQuery(id+"F2.wireOp",EDGE,"E13.35.2"),sQuery(id+"F2.wireOp",EDGE,"E13.35.3"),sQuery(id+"F2.wireOp",EDGE,"E13.35.4")])],"isStart":false}),makeQuery(id+"F3.opExtrude","CAP_FACE",FACE,{"disambiguationData":[OSD([subQ0,sQuery(id+"F2.wireOp",EDGE,"E13.36.0"),sQuery(id+"F2.wireOp",EDGE,"E13.36.1"),sQuery(id+"F2.wireOp",EDGE,"E13.36.2"),sQuery(id+"F2.wireOp",EDGE,"E13.36.3"),sQuery(id+"F2.wireOp",EDGE,"E13.36.4")])],"isStart":false}),makeQuery(id+"F3.opExtrude","CAP_FACE",FACE,{"disambiguationData":[OSD([subQ0,sQuery(id+"F2.wireOp",EDGE,"E13.37.0"),sQuery(id+"F2.wireOp",EDGE,"E13.37.1"),sQuery(id+"F2.wireOp",EDGE,"E13.37.2"),sQuery(id+"F2.wireOp",EDGE,"E13.37.3"),sQuery(id+"F2.wireOp",EDGE,"E13.37.4")])],"isStart":false}),makeQuery(id+"F3.opExtrude","CAP_FACE",FACE,{"disambiguationData":[OSD([subQ0,sQuery(id+"F2.wireOp",EDGE,"E13.38.0"),sQuery(id+"F2.wireOp",EDGE,"E13.38.1"),sQuery(id+"F2.wireOp",EDGE,"E13.38.2"),sQuery(id+"F2.wireOp",EDGE,"E13.38.3"),sQuery(id+"F2.wireOp",EDGE,"E13.38.4")])],"isStart":false}),makeQuery(id+"F3.opExtrude","CAP_FACE",FACE,{"disambiguationData":[OSD([subQ0,sQuery(id+"F2.wireOp",EDGE,"E13.39.0"),sQuery(id+"F2.wireOp",EDGE,"E13.39.1"),sQuery(id+"F2.wireOp",EDGE,"E13.39.2"),sQuery(id+"F2.wireOp",EDGE,"E13.39.3"),sQuery(id+"F2.wireOp",EDGE,"E13.39.4")])],"isStart":false}),makeQuery(id+"F3.opExtrude","CAP_FACE",FACE,{"disambiguationData":[OSD([subQ0,sQuery(id+"F2.wireOp",EDGE,"E13.40.0"),sQuery(id+"F2.wireOp",EDGE,"E13.40.1"),sQuery(id+"F2.wireOp",EDGE,"E13.40.2"),sQuery(id+"F2.wireOp",EDGE,"E13.40.3"),sQuery(id+"F2.wireOp",EDGE,"E13.40.4")])],"isStart":false}),makeQuery(id+"F3.opExtrude","CAP_FACE",FACE,{"disambiguationData":[OSD([subQ0,sQuery(id+"F2.wireOp",EDGE,"E13.41.0"),sQuery(id+"F2.wireOp",EDGE,"E13.41.1"),sQuery(id+"F2.wireOp",EDGE,"E13.41.2"),sQuery(id+"F2.wireOp",EDGE,"E13.41.3"),sQuery(id+"F2.wireOp",EDGE,"E13.41.4")])],"isStart":false}),makeQuery(id+"F3.opExtrude","CAP_FACE",FACE,{"disambiguationData":[OSD([subQ0,sQuery(id+"F2.wireOp",EDGE,"E13.1.0"),sQuery(id+"F2.wireOp",EDGE,"E13.1.1"),sQuery(id+"F2.wireOp",EDGE,"E13.1.2"),sQuery(id+"F2.wireOp",EDGE,"E13.1.3"),sQuery(id+"F2.wireOp",EDGE,"E13.1.4")])],"isStart":false}),makeQuery(id+"F3.opExtrude","CAP_FACE",FACE,{"disambiguationData":[OSD([subQ0,sQuery(id+"F2.wireOp",EDGE,"E13.2.0"),sQuery(id+"F2.wireOp",EDGE,"E13.2.1"),sQuery(id+"F2.wireOp",EDGE,"E13.2.2"),sQuery(id+"F2.wireOp",EDGE,"E13.2.3"),sQuery(id+"F2.wireOp",EDGE,"E13.2.4")])],"isStart":false}),makeQuery(id+"F3.opExtrude","CAP_FACE",FACE,{"disambiguationData":[OSD([subQ0,sQuery(id+"F2.wireOp",EDGE,"E13.3.0"),sQuery(id+"F2.wireOp",EDGE,"E13.3.1"),sQuery(id+"F2.wireOp",EDGE,"E13.3.2"),sQuery(id+"F2.wireOp",EDGE,"E13.3.3"),sQuery(id+"F2.wireOp",EDGE,"E13.3.4")])],"isStart":false}),makeQuery(id+"F3.opExtrude","CAP_FACE",FACE,{"disambiguationData":[OSD([subQ0,sQuery(id+"F2.wireOp",EDGE,"E13.4.0"),sQuery(id+"F2.wireOp",EDGE,"E13.4.1"),sQuery(id+"F2.wireOp",EDGE,"E13.4.2"),sQuery(id+"F2.wireOp",EDGE,"E13.4.3"),sQuery(id+"F2.wireOp",EDGE,"E13.4.4")])],"isStart":false}),makeQuery(id+"F3.opExtrude","CAP_FACE",FACE,{"disambiguationData":[OSD([subQ0,sQuery(id+"F2.wireOp",EDGE,"E13.5.0"),sQuery(id+"F2.wireOp",EDGE,"E13.5.1"),sQuery(id+"F2.wireOp",EDGE,"E13.5.2"),sQuery(id+"F2.wireOp",EDGE,"E13.5.3"),sQuery(id+"F2.wireOp",EDGE,"E13.5.4")])],"isStart":false}),makeQuery(id+"F3.opExtrude","CAP_FACE",FACE,{"disambiguationData":[OSD([subQ0,sQuery(id+"F2.wireOp",EDGE,"E13.6.0"),sQuery(id+"F2.wireOp",EDGE,"E13.6.1"),sQuery(id+"F2.wireOp",EDGE,"E13.6.2"),sQuery(id+"F2.wireOp",EDGE,"E13.6.3"),sQuery(id+"F2.wireOp",EDGE,"E13.6.4")])],"isStart":false}),makeQuery(id+"F3.opExtrude","CAP_FACE",FACE,{"disambiguationData":[OSD([subQ0,sQuery(id+"F2.wireOp",EDGE,"E13.7.0"),sQuery(id+"F2.wireOp",EDGE,"E13.7.1"),sQuery(id+"F2.wireOp",EDGE,"E13.7.2"),sQuery(id+"F2.wireOp",EDGE,"E13.7.3"),sQuery(id+"F2.wireOp",EDGE,"E13.7.4")])],"isStart":false}),makeQuery(id+"F3.opExtrude","CAP_FACE",FACE,{"disambiguationData":[OSD([subQ0,sQuery(id+"F2.wireOp",EDGE,"E13.8.0"),sQuery(id+"F2.wireOp",EDGE,"E13.8.1"),sQuery(id+"F2.wireOp",EDGE,"E13.8.2"),sQuery(id+"F2.wireOp",EDGE,"E13.8.3"),sQuery(id+"F2.wireOp",EDGE,"E13.8.4")])],"isStart":false}),makeQuery(id+"F3.opExtrude","CAP_FACE",FACE,{"disambiguationData":[OSD([subQ0,sQuery(id+"F2.wireOp",EDGE,"E13.9.0"),sQuery(id+"F2.wireOp",EDGE,"E13.9.1"),sQuery(id+"F2.wireOp",EDGE,"E13.9.2"),sQuery(id+"F2.wireOp",EDGE,"E13.9.3"),sQuery(id+"F2.wireOp",EDGE,"E13.9.4")])],"isStart":false}),makeQuery(id+"F3.opExtrude","CAP_FACE",FACE,{"disambiguationData":[OSD([subQ0,sQuery(id+"F2.wireOp",EDGE,"E13.10.0"),sQuery(id+"F2.wireOp",EDGE,"E13.10.1"),sQuery(id+"F2.wireOp",EDGE,"E13.10.2"),sQuery(id+"F2.wireOp",EDGE,"E13.10.3"),sQuery(id+"F2.wireOp",EDGE,"E13.10.4")])],"isStart":false}),makeQuery(id+"F3.opExtrude","CAP_FACE",FACE,{"disambiguationData":[OSD([subQ0,sQuery(id+"F2.wireOp",EDGE,"E13.11.0"),sQuery(id+"F2.wireOp",EDGE,"E13.11.1"),sQuery(id+"F2.wireOp",EDGE,"E13.11.2"),sQuery(id+"F2.wireOp",EDGE,"E13.11.3"),sQuery(id+"F2.wireOp",EDGE,"E13.11.4")])],"isStart":false}),makeQuery(id+"F3.opExtrude","CAP_FACE",FACE,{"disambiguationData":[OSD([subQ0,sQuery(id+"F2.wireOp",EDGE,"E13.12.0"),sQuery(id+"F2.wireOp",EDGE,"E13.12.1"),sQuery(id+"F2.wireOp",EDGE,"E13.12.2"),sQuery(id+"F2.wireOp",EDGE,"E13.12.3"),sQuery(id+"F2.wireOp",EDGE,"E13.12.4")])],"isStart":false}),makeQuery(id+"F3.opExtrude","CAP_FACE",FACE,{"disambiguationData":[OSD([subQ0,sQuery(id+"F2.wireOp",EDGE,"E13.13.0"),sQuery(id+"F2.wireOp",EDGE,"E13.13.1"),sQuery(id+"F2.wireOp",EDGE,"E13.13.2"),sQuery(id+"F2.wireOp",EDGE,"E13.13.3"),sQuery(id+"F2.wireOp",EDGE,"E13.13.4")])],"isStart":false}),makeQuery(id+"F3.opExtrude","CAP_FACE",FACE,{"disambiguationData":[OSD([subQ0,sQuery(id+"F2.wireOp",EDGE,"E13.14.0"),sQuery(id+"F2.wireOp",EDGE,"E13.14.1"),sQuery(id+"F2.wireOp",EDGE,"E13.14.2"),sQuery(id+"F2.wireOp",EDGE,"E13.14.3"),sQuery(id+"F2.wireOp",EDGE,"E13.14.4")])],"isStart":false}),makeQuery(id+"F3.opExtrude","CAP_FACE",FACE,{"disambiguationData":[OSD([subQ0,sQuery(id+"F2.wireOp",EDGE,"E13.15.0"),sQuery(id+"F2.wireOp",EDGE,"E13.15.1"),sQuery(id+"F2.wireOp",EDGE,"E13.15.2"),sQuery(id+"F2.wireOp",EDGE,"E13.15.3"),sQuery(id+"F2.wireOp",EDGE,"E13.15.4")])],"isStart":false}),makeQuery(id+"F3.opExtrude","CAP_FACE",FACE,{"disambiguationData":[OSD([subQ0,sQuery(id+"F2.wireOp",EDGE,"E13.16.0"),sQuery(id+"F2.wireOp",EDGE,"E13.16.1"),sQuery(id+"F2.wireOp",EDGE,"E13.16.2"),sQuery(id+"F2.wireOp",EDGE,"E13.16.3"),sQuery(id+"F2.wireOp",EDGE,"E13.16.4")])],"isStart":false}),makeQuery(id+"F3.opExtrude","CAP_FACE",FACE,{"disambiguationData":[OSD([subQ0,sQuery(id+"F2.wireOp",EDGE,"E13.17.0"),sQuery(id+"F2.wireOp",EDGE,"E13.17.1"),sQuery(id+"F2.wireOp",EDGE,"E13.17.2"),sQuery(id+"F2.wireOp",EDGE,"E13.17.3"),sQuery(id+"F2.wireOp",EDGE,"E13.17.4")])],"isStart":false}),makeQuery(id+"F3.opExtrude","CAP_FACE",FACE,{"disambiguationData":[OSD([subQ0,sQuery(id+"F2.wireOp",EDGE,"E13.18.0"),sQuery(id+"F2.wireOp",EDGE,"E13.18.1"),sQuery(id+"F2.wireOp",EDGE,"E13.18.2"),sQuery(id+"F2.wireOp",EDGE,"E13.18.3"),sQuery(id+"F2.wireOp",EDGE,"E13.18.4")])],"isStart":false}),makeQuery(id+"F3.opExtrude","CAP_FACE",FACE,{"disambiguationData":[OSD([subQ0,sQuery(id+"F2.wireOp",EDGE,"E13.19.0"),sQuery(id+"F2.wireOp",EDGE,"E13.19.1"),sQuery(id+"F2.wireOp",EDGE,"E13.19.2"),sQuery(id+"F2.wireOp",EDGE,"E13.19.3"),sQuery(id+"F2.wireOp",EDGE,"E13.19.4")])],"isStart":false}),makeQuery(id+"F3.opExtrude","CAP_FACE",FACE,{"disambiguationData":[OSD([subQ0,sQuery(id+"F2.wireOp",EDGE,"E13.20.0"),sQuery(id+"F2.wireOp",EDGE,"E13.20.1"),sQuery(id+"F2.wireOp",EDGE,"E13.20.2"),sQuery(id+"F2.wireOp",EDGE,"E13.20.3"),sQuery(id+"F2.wireOp",EDGE,"E13.20.4")])],"isStart":false}),makeQuery(id+"F3.opExtrude","CAP_FACE",FACE,{"disambiguationData":[OSD([subQ0,sQuery(id+"F2.wireOp",EDGE,"E13.21.0"),sQuery(id+"F2.wireOp",EDGE,"E13.21.1"),sQuery(id+"F2.wireOp",EDGE,"E13.21.2"),sQuery(id+"F2.wireOp",EDGE,"E13.21.3"),sQuery(id+"F2.wireOp",EDGE,"E13.21.4")])],"isStart":false}),makeQuery(id+"F3.opExtrude","CAP_FACE",FACE,{"disambiguationData":[OSD([subQ0,sQuery(id+"F2.wireOp",EDGE,"E13.22.0"),sQuery(id+"F2.wireOp",EDGE,"E13.22.1"),sQuery(id+"F2.wireOp",EDGE,"E13.22.2"),sQuery(id+"F2.wireOp",EDGE,"E13.22.3"),sQuery(id+"F2.wireOp",EDGE,"E13.22.4")])],"isStart":false}),makeQuery(id+"F3.opExtrude","CAP_FACE",FACE,{"disambiguationData":[OSD([subQ0,sQuery(id+"F2.wireOp",EDGE,"E13.23.0"),sQuery(id+"F2.wireOp",EDGE,"E13.23.1"),sQuery(id+"F2.wireOp",EDGE,"E13.23.2"),sQuery(id+"F2.wireOp",EDGE,"E13.23.3"),sQuery(id+"F2.wireOp",EDGE,"E13.23.4")])],"isStart":false}),makeQuery(id+"F3.opExtrude","CAP_FACE",FACE,{"disambiguationData":[OSD([subQ0,sQuery(id+"F2.wireOp",EDGE,"E13.24.0"),sQuery(id+"F2.wireOp",EDGE,"E13.24.1"),sQuery(id+"F2.wireOp",EDGE,"E13.24.2"),sQuery(id+"F2.wireOp",EDGE,"E13.24.3"),sQuery(id+"F2.wireOp",EDGE,"E13.24.4")])],"isStart":false}),makeQuery(id+"F3.opExtrude","CAP_FACE",FACE,{"disambiguationData":[OSD([subQ0,sQuery(id+"F2.wireOp",EDGE,"E13.25.0"),sQuery(id+"F2.wireOp",EDGE,"E13.25.1"),sQuery(id+"F2.wireOp",EDGE,"E13.25.2"),sQuery(id+"F2.wireOp",EDGE,"E13.25.3"),sQuery(id+"F2.wireOp",EDGE,"E13.25.4")])],"isStart":false}),makeQuery(id+"F3.opExtrude","CAP_FACE",FACE,{"disambiguationData":[OSD([subQ0,sQuery(id+"F2.wireOp",EDGE,"E13.26.0"),sQuery(id+"F2.wireOp",EDGE,"E13.26.1"),sQuery(id+"F2.wireOp",EDGE,"E13.26.2"),sQuery(id+"F2.wireOp",EDGE,"E13.26.3"),sQuery(id+"F2.wireOp",EDGE,"E13.26.4")])],"isStart":false}),makeQuery(id+"F3.opExtrude","CAP_FACE",FACE,{"disambiguationData":[OSD([subQ0,sQuery(id+"F2.wireOp",EDGE,"E13.27.0"),sQuery(id+"F2.wireOp",EDGE,"E13.27.1"),sQuery(id+"F2.wireOp",EDGE,"E13.27.2"),sQuery(id+"F2.wireOp",EDGE,"E13.27.3"),sQuery(id+"F2.wireOp",EDGE,"E13.27.4")])],"isStart":false}),makeQuery(id+"F3.opExtrude","CAP_FACE",FACE,{"disambiguationData":[OSD([subQ0,sQuery(id+"F2.wireOp",EDGE,"E13.28.0"),sQuery(id+"F2.wireOp",EDGE,"E13.28.1"),sQuery(id+"F2.wireOp",EDGE,"E13.28.2"),sQuery(id+"F2.wireOp",EDGE,"E13.28.3"),sQuery(id+"F2.wireOp",EDGE,"E13.28.4")])],"isStart":false}),makeQuery(id+"F3.opExtrude","CAP_FACE",FACE,{"disambiguationData":[OSD([subQ0,sQuery(id+"F2.wireOp",EDGE,"E13.29.0"),sQuery(id+"F2.wireOp",EDGE,"E13.29.1"),sQuery(id+"F2.wireOp",EDGE,"E13.29.2"),sQuery(id+"F2.wireOp",EDGE,"E13.29.3"),sQuery(id+"F2.wireOp",EDGE,"E13.29.4")])],"isStart":false}),makeQuery(id+"F3.opExtrude","CAP_FACE",FACE,{"disambiguationData":[OSD([subQ0,sQuery(id+"F2.wireOp",EDGE,"E13.30.0"),sQuery(id+"F2.wireOp",EDGE,"E13.30.1"),sQuery(id+"F2.wireOp",EDGE,"E13.30.2"),sQuery(id+"F2.wireOp",EDGE,"E13.30.3"),sQuery(id+"F2.wireOp",EDGE,"E13.30.4")])],"isStart":false}),makeQuery(id+"F3.opExtrude","CAP_FACE",FACE,{"disambiguationData":[OSD([subQ0,sQuery(id+"F2.wireOp",EDGE,"E13.31.0"),sQuery(id+"F2.wireOp",EDGE,"E13.31.1"),sQuery(id+"F2.wireOp",EDGE,"E13.31.2"),sQuery(id+"F2.wireOp",EDGE,"E13.31.3"),sQuery(id+"F2.wireOp",EDGE,"E13.31.4")])],"isStart":false})]});}
            var sketch = newSketch(context, id + "F4", { "sketchPlane" : qUnion([Q0])});
            skCircle(sketch, "E14", {"center": v(0, 0) * mm, "radius": 9 * mm});
            skSolve(sketch);
        }
        {
            var Q0;
            Q0=qSketchRegion(id+"F4",true);
            extrude(context, id + "F5", {"entities" : qUnion([Q0]), "operationType" : NewBodyOperationType.REMOVE, "oppositeDirection" : true, "depth" : 0.2 * mm});
        }
        {
            var Q0;
            {var subQ0=sQuery(id+"F2.wireOp",EDGE,"E4");Q0=makeQuery(id+"F3.boolean.opBoolean","MERGE",FACE,{"derivedFrom":[makeQuery(id+"F1.opExtrude","CAP_FACE",FACE,{"disambiguationData":[OSD([sQuery(id+"F0.wireOp",EDGE,"E0")])],"isStart":true}),makeQuery(id+"F3.opExtrude","CAP_FACE",FACE,{"disambiguationData":[OSD([sQuery(id+"F2.wireOp",EDGE,"E2"),subQ0,sQuery(id+"F2.wireOp",EDGE,"E7"),sQuery(id+"F2.wireOp",EDGE,"E8"),sQuery(id+"F2.wireOp",EDGE,"E9"),sQuery(id+"F2.wireOp",EDGE,"E12")])],"isStart":true}),makeQuery(id+"F3.opExtrude","CAP_FACE",FACE,{"disambiguationData":[OSD([subQ0,sQuery(id+"F2.wireOp",EDGE,"E13.32.0"),sQuery(id+"F2.wireOp",EDGE,"E13.32.1"),sQuery(id+"F2.wireOp",EDGE,"E13.32.2"),sQuery(id+"F2.wireOp",EDGE,"E13.32.3"),sQuery(id+"F2.wireOp",EDGE,"E13.32.4")])],"isStart":true}),makeQuery(id+"F3.opExtrude","CAP_FACE",FACE,{"disambiguationData":[OSD([subQ0,sQuery(id+"F2.wireOp",EDGE,"E13.33.0"),sQuery(id+"F2.wireOp",EDGE,"E13.33.1"),sQuery(id+"F2.wireOp",EDGE,"E13.33.2"),sQuery(id+"F2.wireOp",EDGE,"E13.33.3"),sQuery(id+"F2.wireOp",EDGE,"E13.33.4")])],"isStart":true}),makeQuery(id+"F3.opExtrude","CAP_FACE",FACE,{"disambiguationData":[OSD([subQ0,sQuery(id+"F2.wireOp",EDGE,"E13.34.0"),sQuery(id+"F2.wireOp",EDGE,"E13.34.1"),sQuery(id+"F2.wireOp",EDGE,"E13.34.2"),sQuery(id+"F2.wireOp",EDGE,"E13.34.3"),sQuery(id+"F2.wireOp",EDGE,"E13.34.4")])],"isStart":true}),makeQuery(id+"F3.opExtrude","CAP_FACE",FACE,{"disambiguationData":[OSD([subQ0,sQuery(id+"F2.wireOp",EDGE,"E13.35.0"),sQuery(id+"F2.wireOp",EDGE,"E13.35.1"),sQuery(id+"F2.wireOp",EDGE,"E13.35.2"),sQuery(id+"F2.wireOp",EDGE,"E13.35.3"),sQuery(id+"F2.wireOp",EDGE,"E13.35.4")])],"isStart":true}),makeQuery(id+"F3.opExtrude","CAP_FACE",FACE,{"disambiguationData":[OSD([subQ0,sQuery(id+"F2.wireOp",EDGE,"E13.36.0"),sQuery(id+"F2.wireOp",EDGE,"E13.36.1"),sQuery(id+"F2.wireOp",EDGE,"E13.36.2"),sQuery(id+"F2.wireOp",EDGE,"E13.36.3"),sQuery(id+"F2.wireOp",EDGE,"E13.36.4")])],"isStart":true}),makeQuery(id+"F3.opExtrude","CAP_FACE",FACE,{"disambiguationData":[OSD([subQ0,sQuery(id+"F2.wireOp",EDGE,"E13.37.0"),sQuery(id+"F2.wireOp",EDGE,"E13.37.1"),sQuery(id+"F2.wireOp",EDGE,"E13.37.2"),sQuery(id+"F2.wireOp",EDGE,"E13.37.3"),sQuery(id+"F2.wireOp",EDGE,"E13.37.4")])],"isStart":true}),makeQuery(id+"F3.opExtrude","CAP_FACE",FACE,{"disambiguationData":[OSD([subQ0,sQuery(id+"F2.wireOp",EDGE,"E13.38.0"),sQuery(id+"F2.wireOp",EDGE,"E13.38.1"),sQuery(id+"F2.wireOp",EDGE,"E13.38.2"),sQuery(id+"F2.wireOp",EDGE,"E13.38.3"),sQuery(id+"F2.wireOp",EDGE,"E13.38.4")])],"isStart":true}),makeQuery(id+"F3.opExtrude","CAP_FACE",FACE,{"disambiguationData":[OSD([subQ0,sQuery(id+"F2.wireOp",EDGE,"E13.39.0"),sQuery(id+"F2.wireOp",EDGE,"E13.39.1"),sQuery(id+"F2.wireOp",EDGE,"E13.39.2"),sQuery(id+"F2.wireOp",EDGE,"E13.39.3"),sQuery(id+"F2.wireOp",EDGE,"E13.39.4")])],"isStart":true}),makeQuery(id+"F3.opExtrude","CAP_FACE",FACE,{"disambiguationData":[OSD([subQ0,sQuery(id+"F2.wireOp",EDGE,"E13.40.0"),sQuery(id+"F2.wireOp",EDGE,"E13.40.1"),sQuery(id+"F2.wireOp",EDGE,"E13.40.2"),sQuery(id+"F2.wireOp",EDGE,"E13.40.3"),sQuery(id+"F2.wireOp",EDGE,"E13.40.4")])],"isStart":true}),makeQuery(id+"F3.opExtrude","CAP_FACE",FACE,{"disambiguationData":[OSD([subQ0,sQuery(id+"F2.wireOp",EDGE,"E13.41.0"),sQuery(id+"F2.wireOp",EDGE,"E13.41.1"),sQuery(id+"F2.wireOp",EDGE,"E13.41.2"),sQuery(id+"F2.wireOp",EDGE,"E13.41.3"),sQuery(id+"F2.wireOp",EDGE,"E13.41.4")])],"isStart":true}),makeQuery(id+"F3.opExtrude","CAP_FACE",FACE,{"disambiguationData":[OSD([subQ0,sQuery(id+"F2.wireOp",EDGE,"E13.1.0"),sQuery(id+"F2.wireOp",EDGE,"E13.1.1"),sQuery(id+"F2.wireOp",EDGE,"E13.1.2"),sQuery(id+"F2.wireOp",EDGE,"E13.1.3"),sQuery(id+"F2.wireOp",EDGE,"E13.1.4")])],"isStart":true}),makeQuery(id+"F3.opExtrude","CAP_FACE",FACE,{"disambiguationData":[OSD([subQ0,sQuery(id+"F2.wireOp",EDGE,"E13.2.0"),sQuery(id+"F2.wireOp",EDGE,"E13.2.1"),sQuery(id+"F2.wireOp",EDGE,"E13.2.2"),sQuery(id+"F2.wireOp",EDGE,"E13.2.3"),sQuery(id+"F2.wireOp",EDGE,"E13.2.4")])],"isStart":true}),makeQuery(id+"F3.opExtrude","CAP_FACE",FACE,{"disambiguationData":[OSD([subQ0,sQuery(id+"F2.wireOp",EDGE,"E13.3.0"),sQuery(id+"F2.wireOp",EDGE,"E13.3.1"),sQuery(id+"F2.wireOp",EDGE,"E13.3.2"),sQuery(id+"F2.wireOp",EDGE,"E13.3.3"),sQuery(id+"F2.wireOp",EDGE,"E13.3.4")])],"isStart":true}),makeQuery(id+"F3.opExtrude","CAP_FACE",FACE,{"disambiguationData":[OSD([subQ0,sQuery(id+"F2.wireOp",EDGE,"E13.4.0"),sQuery(id+"F2.wireOp",EDGE,"E13.4.1"),sQuery(id+"F2.wireOp",EDGE,"E13.4.2"),sQuery(id+"F2.wireOp",EDGE,"E13.4.3"),sQuery(id+"F2.wireOp",EDGE,"E13.4.4")])],"isStart":true}),makeQuery(id+"F3.opExtrude","CAP_FACE",FACE,{"disambiguationData":[OSD([subQ0,sQuery(id+"F2.wireOp",EDGE,"E13.5.0"),sQuery(id+"F2.wireOp",EDGE,"E13.5.1"),sQuery(id+"F2.wireOp",EDGE,"E13.5.2"),sQuery(id+"F2.wireOp",EDGE,"E13.5.3"),sQuery(id+"F2.wireOp",EDGE,"E13.5.4")])],"isStart":true}),makeQuery(id+"F3.opExtrude","CAP_FACE",FACE,{"disambiguationData":[OSD([subQ0,sQuery(id+"F2.wireOp",EDGE,"E13.6.0"),sQuery(id+"F2.wireOp",EDGE,"E13.6.1"),sQuery(id+"F2.wireOp",EDGE,"E13.6.2"),sQuery(id+"F2.wireOp",EDGE,"E13.6.3"),sQuery(id+"F2.wireOp",EDGE,"E13.6.4")])],"isStart":true}),makeQuery(id+"F3.opExtrude","CAP_FACE",FACE,{"disambiguationData":[OSD([subQ0,sQuery(id+"F2.wireOp",EDGE,"E13.7.0"),sQuery(id+"F2.wireOp",EDGE,"E13.7.1"),sQuery(id+"F2.wireOp",EDGE,"E13.7.2"),sQuery(id+"F2.wireOp",EDGE,"E13.7.3"),sQuery(id+"F2.wireOp",EDGE,"E13.7.4")])],"isStart":true}),makeQuery(id+"F3.opExtrude","CAP_FACE",FACE,{"disambiguationData":[OSD([subQ0,sQuery(id+"F2.wireOp",EDGE,"E13.8.0"),sQuery(id+"F2.wireOp",EDGE,"E13.8.1"),sQuery(id+"F2.wireOp",EDGE,"E13.8.2"),sQuery(id+"F2.wireOp",EDGE,"E13.8.3"),sQuery(id+"F2.wireOp",EDGE,"E13.8.4")])],"isStart":true}),makeQuery(id+"F3.opExtrude","CAP_FACE",FACE,{"disambiguationData":[OSD([subQ0,sQuery(id+"F2.wireOp",EDGE,"E13.9.0"),sQuery(id+"F2.wireOp",EDGE,"E13.9.1"),sQuery(id+"F2.wireOp",EDGE,"E13.9.2"),sQuery(id+"F2.wireOp",EDGE,"E13.9.3"),sQuery(id+"F2.wireOp",EDGE,"E13.9.4")])],"isStart":true}),makeQuery(id+"F3.opExtrude","CAP_FACE",FACE,{"disambiguationData":[OSD([subQ0,sQuery(id+"F2.wireOp",EDGE,"E13.10.0"),sQuery(id+"F2.wireOp",EDGE,"E13.10.1"),sQuery(id+"F2.wireOp",EDGE,"E13.10.2"),sQuery(id+"F2.wireOp",EDGE,"E13.10.3"),sQuery(id+"F2.wireOp",EDGE,"E13.10.4")])],"isStart":true}),makeQuery(id+"F3.opExtrude","CAP_FACE",FACE,{"disambiguationData":[OSD([subQ0,sQuery(id+"F2.wireOp",EDGE,"E13.11.0"),sQuery(id+"F2.wireOp",EDGE,"E13.11.1"),sQuery(id+"F2.wireOp",EDGE,"E13.11.2"),sQuery(id+"F2.wireOp",EDGE,"E13.11.3"),sQuery(id+"F2.wireOp",EDGE,"E13.11.4")])],"isStart":true}),makeQuery(id+"F3.opExtrude","CAP_FACE",FACE,{"disambiguationData":[OSD([subQ0,sQuery(id+"F2.wireOp",EDGE,"E13.12.0"),sQuery(id+"F2.wireOp",EDGE,"E13.12.1"),sQuery(id+"F2.wireOp",EDGE,"E13.12.2"),sQuery(id+"F2.wireOp",EDGE,"E13.12.3"),sQuery(id+"F2.wireOp",EDGE,"E13.12.4")])],"isStart":true}),makeQuery(id+"F3.opExtrude","CAP_FACE",FACE,{"disambiguationData":[OSD([subQ0,sQuery(id+"F2.wireOp",EDGE,"E13.13.0"),sQuery(id+"F2.wireOp",EDGE,"E13.13.1"),sQuery(id+"F2.wireOp",EDGE,"E13.13.2"),sQuery(id+"F2.wireOp",EDGE,"E13.13.3"),sQuery(id+"F2.wireOp",EDGE,"E13.13.4")])],"isStart":true}),makeQuery(id+"F3.opExtrude","CAP_FACE",FACE,{"disambiguationData":[OSD([subQ0,sQuery(id+"F2.wireOp",EDGE,"E13.14.0"),sQuery(id+"F2.wireOp",EDGE,"E13.14.1"),sQuery(id+"F2.wireOp",EDGE,"E13.14.2"),sQuery(id+"F2.wireOp",EDGE,"E13.14.3"),sQuery(id+"F2.wireOp",EDGE,"E13.14.4")])],"isStart":true}),makeQuery(id+"F3.opExtrude","CAP_FACE",FACE,{"disambiguationData":[OSD([subQ0,sQuery(id+"F2.wireOp",EDGE,"E13.15.0"),sQuery(id+"F2.wireOp",EDGE,"E13.15.1"),sQuery(id+"F2.wireOp",EDGE,"E13.15.2"),sQuery(id+"F2.wireOp",EDGE,"E13.15.3"),sQuery(id+"F2.wireOp",EDGE,"E13.15.4")])],"isStart":true}),makeQuery(id+"F3.opExtrude","CAP_FACE",FACE,{"disambiguationData":[OSD([subQ0,sQuery(id+"F2.wireOp",EDGE,"E13.16.0"),sQuery(id+"F2.wireOp",EDGE,"E13.16.1"),sQuery(id+"F2.wireOp",EDGE,"E13.16.2"),sQuery(id+"F2.wireOp",EDGE,"E13.16.3"),sQuery(id+"F2.wireOp",EDGE,"E13.16.4")])],"isStart":true}),makeQuery(id+"F3.opExtrude","CAP_FACE",FACE,{"disambiguationData":[OSD([subQ0,sQuery(id+"F2.wireOp",EDGE,"E13.17.0"),sQuery(id+"F2.wireOp",EDGE,"E13.17.1"),sQuery(id+"F2.wireOp",EDGE,"E13.17.2"),sQuery(id+"F2.wireOp",EDGE,"E13.17.3"),sQuery(id+"F2.wireOp",EDGE,"E13.17.4")])],"isStart":true}),makeQuery(id+"F3.opExtrude","CAP_FACE",FACE,{"disambiguationData":[OSD([subQ0,sQuery(id+"F2.wireOp",EDGE,"E13.18.0"),sQuery(id+"F2.wireOp",EDGE,"E13.18.1"),sQuery(id+"F2.wireOp",EDGE,"E13.18.2"),sQuery(id+"F2.wireOp",EDGE,"E13.18.3"),sQuery(id+"F2.wireOp",EDGE,"E13.18.4")])],"isStart":true}),makeQuery(id+"F3.opExtrude","CAP_FACE",FACE,{"disambiguationData":[OSD([subQ0,sQuery(id+"F2.wireOp",EDGE,"E13.19.0"),sQuery(id+"F2.wireOp",EDGE,"E13.19.1"),sQuery(id+"F2.wireOp",EDGE,"E13.19.2"),sQuery(id+"F2.wireOp",EDGE,"E13.19.3"),sQuery(id+"F2.wireOp",EDGE,"E13.19.4")])],"isStart":true}),makeQuery(id+"F3.opExtrude","CAP_FACE",FACE,{"disambiguationData":[OSD([subQ0,sQuery(id+"F2.wireOp",EDGE,"E13.20.0"),sQuery(id+"F2.wireOp",EDGE,"E13.20.1"),sQuery(id+"F2.wireOp",EDGE,"E13.20.2"),sQuery(id+"F2.wireOp",EDGE,"E13.20.3"),sQuery(id+"F2.wireOp",EDGE,"E13.20.4")])],"isStart":true}),makeQuery(id+"F3.opExtrude","CAP_FACE",FACE,{"disambiguationData":[OSD([subQ0,sQuery(id+"F2.wireOp",EDGE,"E13.21.0"),sQuery(id+"F2.wireOp",EDGE,"E13.21.1"),sQuery(id+"F2.wireOp",EDGE,"E13.21.2"),sQuery(id+"F2.wireOp",EDGE,"E13.21.3"),sQuery(id+"F2.wireOp",EDGE,"E13.21.4")])],"isStart":true}),makeQuery(id+"F3.opExtrude","CAP_FACE",FACE,{"disambiguationData":[OSD([subQ0,sQuery(id+"F2.wireOp",EDGE,"E13.22.0"),sQuery(id+"F2.wireOp",EDGE,"E13.22.1"),sQuery(id+"F2.wireOp",EDGE,"E13.22.2"),sQuery(id+"F2.wireOp",EDGE,"E13.22.3"),sQuery(id+"F2.wireOp",EDGE,"E13.22.4")])],"isStart":true}),makeQuery(id+"F3.opExtrude","CAP_FACE",FACE,{"disambiguationData":[OSD([subQ0,sQuery(id+"F2.wireOp",EDGE,"E13.23.0"),sQuery(id+"F2.wireOp",EDGE,"E13.23.1"),sQuery(id+"F2.wireOp",EDGE,"E13.23.2"),sQuery(id+"F2.wireOp",EDGE,"E13.23.3"),sQuery(id+"F2.wireOp",EDGE,"E13.23.4")])],"isStart":true}),makeQuery(id+"F3.opExtrude","CAP_FACE",FACE,{"disambiguationData":[OSD([subQ0,sQuery(id+"F2.wireOp",EDGE,"E13.24.0"),sQuery(id+"F2.wireOp",EDGE,"E13.24.1"),sQuery(id+"F2.wireOp",EDGE,"E13.24.2"),sQuery(id+"F2.wireOp",EDGE,"E13.24.3"),sQuery(id+"F2.wireOp",EDGE,"E13.24.4")])],"isStart":true}),makeQuery(id+"F3.opExtrude","CAP_FACE",FACE,{"disambiguationData":[OSD([subQ0,sQuery(id+"F2.wireOp",EDGE,"E13.25.0"),sQuery(id+"F2.wireOp",EDGE,"E13.25.1"),sQuery(id+"F2.wireOp",EDGE,"E13.25.2"),sQuery(id+"F2.wireOp",EDGE,"E13.25.3"),sQuery(id+"F2.wireOp",EDGE,"E13.25.4")])],"isStart":true}),makeQuery(id+"F3.opExtrude","CAP_FACE",FACE,{"disambiguationData":[OSD([subQ0,sQuery(id+"F2.wireOp",EDGE,"E13.26.0"),sQuery(id+"F2.wireOp",EDGE,"E13.26.1"),sQuery(id+"F2.wireOp",EDGE,"E13.26.2"),sQuery(id+"F2.wireOp",EDGE,"E13.26.3"),sQuery(id+"F2.wireOp",EDGE,"E13.26.4")])],"isStart":true}),makeQuery(id+"F3.opExtrude","CAP_FACE",FACE,{"disambiguationData":[OSD([subQ0,sQuery(id+"F2.wireOp",EDGE,"E13.27.0"),sQuery(id+"F2.wireOp",EDGE,"E13.27.1"),sQuery(id+"F2.wireOp",EDGE,"E13.27.2"),sQuery(id+"F2.wireOp",EDGE,"E13.27.3"),sQuery(id+"F2.wireOp",EDGE,"E13.27.4")])],"isStart":true}),makeQuery(id+"F3.opExtrude","CAP_FACE",FACE,{"disambiguationData":[OSD([subQ0,sQuery(id+"F2.wireOp",EDGE,"E13.28.0"),sQuery(id+"F2.wireOp",EDGE,"E13.28.1"),sQuery(id+"F2.wireOp",EDGE,"E13.28.2"),sQuery(id+"F2.wireOp",EDGE,"E13.28.3"),sQuery(id+"F2.wireOp",EDGE,"E13.28.4")])],"isStart":true}),makeQuery(id+"F3.opExtrude","CAP_FACE",FACE,{"disambiguationData":[OSD([subQ0,sQuery(id+"F2.wireOp",EDGE,"E13.29.0"),sQuery(id+"F2.wireOp",EDGE,"E13.29.1"),sQuery(id+"F2.wireOp",EDGE,"E13.29.2"),sQuery(id+"F2.wireOp",EDGE,"E13.29.3"),sQuery(id+"F2.wireOp",EDGE,"E13.29.4")])],"isStart":true}),makeQuery(id+"F3.opExtrude","CAP_FACE",FACE,{"disambiguationData":[OSD([subQ0,sQuery(id+"F2.wireOp",EDGE,"E13.30.0"),sQuery(id+"F2.wireOp",EDGE,"E13.30.1"),sQuery(id+"F2.wireOp",EDGE,"E13.30.2"),sQuery(id+"F2.wireOp",EDGE,"E13.30.3"),sQuery(id+"F2.wireOp",EDGE,"E13.30.4")])],"isStart":true}),makeQuery(id+"F3.opExtrude","CAP_FACE",FACE,{"disambiguationData":[OSD([subQ0,sQuery(id+"F2.wireOp",EDGE,"E13.31.0"),sQuery(id+"F2.wireOp",EDGE,"E13.31.1"),sQuery(id+"F2.wireOp",EDGE,"E13.31.2"),sQuery(id+"F2.wireOp",EDGE,"E13.31.3"),sQuery(id+"F2.wireOp",EDGE,"E13.31.4")])],"isStart":true})]});}
            var sketch = newSketch(context, id + "F6", { "sketchPlane" : qUnion([Q0])});
            skCircle(sketch, "E15", {"center": v(0, 0) * mm, "radius": 9 * mm});
            skSolve(sketch);
        }
        {
            var Q0;
            Q0=qSketchRegion(id+"F6",true);
            extrude(context, id + "F7", {"entities" : qUnion([Q0]), "operationType" : NewBodyOperationType.REMOVE, "oppositeDirection" : true, "depth" : 0.5 * mm});
        }
        {
            var Q0;
            Q0=makeQuery(id+"F5.boolean.opBoolean","COPY",FACE,{"derivedFrom":makeQuery(id+"F5.opExtrude","CAP_FACE",FACE,{"disambiguationData":[OSD([sQuery(id+"F4.wireOp",EDGE,"E14")])],"isStart":false})});
            var sketch = newSketch(context, id + "F8", { "sketchPlane" : qUnion([Q0])});
            skCircle(sketch, "E16.cCircle", {"center": v(0, 0) * mm, "radius": 3.5 * mm, "construction": true});
            skLineSegment(sketch, "E16.0", {"start": v(-2.02, 3.5) * mm, "end": v(2.02, 3.5) * mm});
            skLineSegment(sketch, "E16.1", {"start": v(2.02, 3.5) * mm, "end": v(4.04, 0) * mm});
            skLineSegment(sketch, "E16.2", {"start": v(4.04, 0) * mm, "end": v(2.02, -3.5) * mm});
            skLineSegment(sketch, "E16.3", {"start": v(2.02, -3.5) * mm, "end": v(-2.02, -3.5) * mm});
            skLineSegment(sketch, "E16.4", {"start": v(-2.02, -3.5) * mm, "end": v(-4.04, 0) * mm});
            skLineSegment(sketch, "E16.5", {"start": v(-4.04, 0) * mm, "end": v(-2.02, 3.5) * mm});
            skPoint(sketch, "E16.0.midPoint", {"position": v(0, 3.5) * mm});
            skCircle(sketch, "E17.cCircle", {"center": v(0, 0) * mm, "radius": 5 * mm, "construction": true});
            skLineSegment(sketch, "E17.0", {"start": v(-2.89, 5) * mm, "end": v(2.89, 5) * mm});
            skLineSegment(sketch, "E17.1", {"start": v(2.89, 5) * mm, "end": v(5.77, 0) * mm});
            skLineSegment(sketch, "E17.2", {"start": v(5.77, 0) * mm, "end": v(2.89, -5) * mm});
            skLineSegment(sketch, "E17.3", {"start": v(2.89, -5) * mm, "end": v(-2.89, -5) * mm});
            skLineSegment(sketch, "E17.4", {"start": v(-2.89, -5) * mm, "end": v(-5.77, 0) * mm});
            skLineSegment(sketch, "E17.5", {"start": v(-5.77, 0) * mm, "end": v(-2.89, 5) * mm});
            skPoint(sketch, "E17.0.midPoint", {"position": v(0, 5) * mm});
            skSolve(sketch);
        }
        {
            var Q0;
            Q0=makeQuery(id+"F8.imprint","IMPRINT",FACE,{"disambiguationData":[TD([[makeQuery(id+"F8.imprint","IMPRINT",EDGE,{"derivedFrom":sQuery(id+"F8.wireOp",EDGE,"E16.0")}),1.0]])]});
            extrude(context, id + "F9", {"entities" : qUnion([Q0]), "operationType" : NewBodyOperationType.ADD, "depth" : 2.7 * mm});
        }
        {
            var Q0;
            Q0=makeQuery(id+"F9.opExtrude","CAP_FACE",FACE,{"disambiguationData":[OSD([sQuery(id+"F8.wireOp",EDGE,"E16.0"),sQuery(id+"F8.wireOp",EDGE,"E16.1"),sQuery(id+"F8.wireOp",EDGE,"E16.2"),sQuery(id+"F8.wireOp",EDGE,"E16.3"),sQuery(id+"F8.wireOp",EDGE,"E16.4"),sQuery(id+"F8.wireOp",EDGE,"E16.5"),sQuery(id+"F8.wireOp",EDGE,"E17.0"),sQuery(id+"F8.wireOp",EDGE,"E17.1"),sQuery(id+"F8.wireOp",EDGE,"E17.2"),sQuery(id+"F8.wireOp",EDGE,"E17.3"),sQuery(id+"F8.wireOp",EDGE,"E17.4"),sQuery(id+"F8.wireOp",EDGE,"E17.5")])],"isStart":false});
            var sketch = newSketch(context, id + "F10", { "sketchPlane" : qUnion([Q0])});
            skLineSegment(sketch, "E18.bottom", {"start": v(-1.75, 5) * mm, "end": v(1.75, 5) * mm});
            skLineSegment(sketch, "E18.top", {"start": v(-1.75, 3.5) * mm, "end": v(1.75, 3.5) * mm});
            skLineSegment(sketch, "E18.left", {"start": v(-1.75, 5) * mm, "end": v(-1.75, 3.5) * mm});
            skLineSegment(sketch, "E18.right", {"start": v(1.75, 5) * mm, "end": v(1.75, 3.5) * mm});
            skSolve(sketch);
        }
        {
            var Q0;
            Q0 = qSketchRegion(id + "F10", true);
            extrude(context, id + "F11", {"entities" : qUnion([Q0]), "operationType" : NewBodyOperationType.REMOVE, "oppositeDirection" : true, "depth" : 2.5 * mm});
        }
        {
            var Q0;
            Q0=makeQuery(id+"F9.boolean.opBoolean","SPLIT",FACE,{"disambiguationData":[TD([makeQuery(id+"F9.opExtrude","SWEPT_FACE",FACE,{"disambiguationData":[OSD([sQuery(id+"F8.wireOp",EDGE,"E16.0")])]})])],"derivedFrom":makeQuery(id+"F5.boolean.opBoolean","COPY",FACE,{"derivedFrom":makeQuery(id+"F5.opExtrude","CAP_FACE",FACE,{"disambiguationData":[OSD([sQuery(id+"F4.wireOp",EDGE,"E14")])],"isStart":false})})});
            var sketch = newSketch(context, id + "F12", { "sketchPlane" : qUnion([Q0])});
            skCircle(sketch, "E19", {"center": v(0, 0) * mm, "radius": 1.5 * mm});
            skSolve(sketch);
        }
        {
            var Q0;
            Q0 = qSketchRegion(id + "F12", true);
            extrude(context, id + "F13", {"entities" : qUnion([Q0]), "operationType" : NewBodyOperationType.REMOVE, "oppositeDirection" : true, "depth" : 25 * mm});
        }
        {
            var Q0;
            Q0=makeQuery(id+"F9.opExtrude","SWEPT_EDGE",EDGE,{"disambiguationData":[OSD([sQuery(id+"F8.wireOp",EDGE,"E17.3"),sQuery(id+"F8.wireOp",EDGE,"E17.4")])]});
            var Q1;
            Q1=makeQuery(id+"F9.opExtrude","SWEPT_EDGE",EDGE,{"disambiguationData":[OSD([sQuery(id+"F8.wireOp",EDGE,"E17.4"),sQuery(id+"F8.wireOp",EDGE,"E17.5")])]});
            var Q2;
            Q2=makeQuery(id+"F9.opExtrude","SWEPT_EDGE",EDGE,{"disambiguationData":[OSD([sQuery(id+"F8.wireOp",EDGE,"E17.0"),sQuery(id+"F8.wireOp",EDGE,"E17.5")])]});
            var Q3;
            Q3=makeQuery(id+"F9.opExtrude","SWEPT_EDGE",EDGE,{"disambiguationData":[OSD([sQuery(id+"F8.wireOp",EDGE,"E17.0"),sQuery(id+"F8.wireOp",EDGE,"E17.1")])]});
            var Q4;
            Q4=makeQuery(id+"F9.opExtrude","SWEPT_EDGE",EDGE,{"disambiguationData":[OSD([sQuery(id+"F8.wireOp",EDGE,"E17.1"),sQuery(id+"F8.wireOp",EDGE,"E17.2")])]});
            var Q5;
            Q5=makeQuery(id+"F9.opExtrude","SWEPT_EDGE",EDGE,{"disambiguationData":[OSD([sQuery(id+"F8.wireOp",EDGE,"E17.2"),sQuery(id+"F8.wireOp",EDGE,"E17.3")])]});
            fillet(context, id + "F14", {"entities" : qUnion([Q0, Q1, Q2, Q3, Q4, Q5]), "radius" : 1 * mm, "tangentPropagation" : true, "allowEdgeOverflow" : false});
        }
        {
            var Q0;
            Q0=makeQuery(id+"F9.opExtrude","CAP_EDGE",EDGE,{"disambiguationData":[OSD([sQuery(id+"F8.wireOp",EDGE,"E17.4")])],"isStart":false});
            fillet(context, id + "F15", {"entities" : qUnion([Q0]), "radius" : 0.3 * mm, "tangentPropagation" : true, "allowEdgeOverflow" : false});
        }
    });
